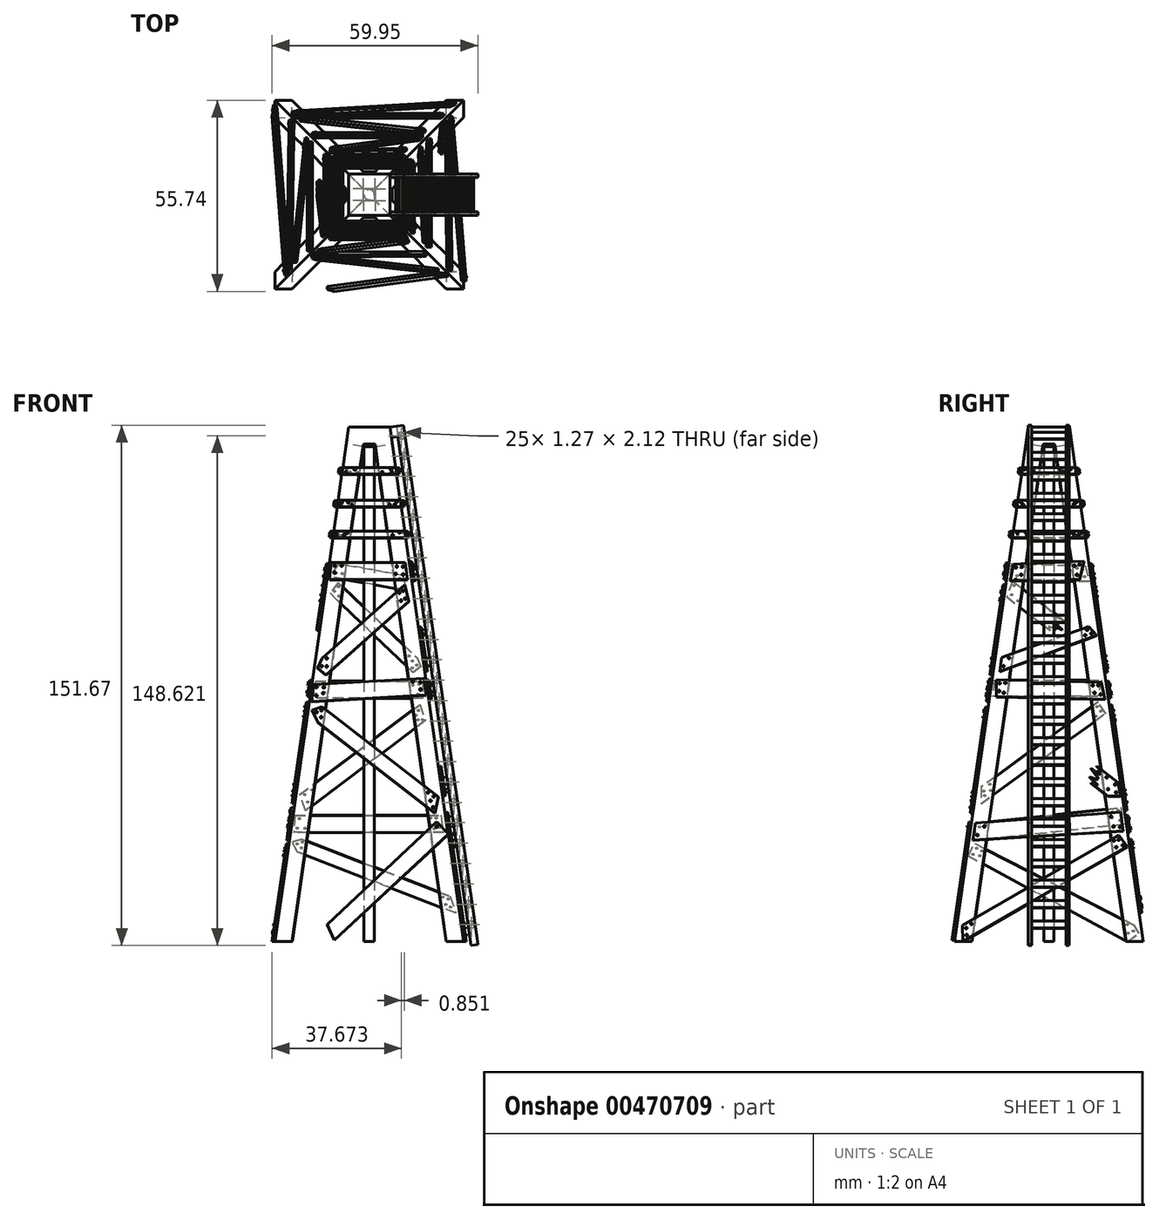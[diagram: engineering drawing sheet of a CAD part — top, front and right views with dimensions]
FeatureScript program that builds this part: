
annotation { "Feature Type Name" : "Feature", "Feature Type Description" : "" }
export const myFeature = defineFeature(function(context is Context, id is Id, definition is map)
    precondition{}
    {
        {
            var Q0;
            Q0=qCreatedBy(makeId("Top.planeOp"),FACE);
            var sketch = newSketch(context, id + "F0", { "sketchPlane" : qUnion([Q0])});
            skCircle(sketch, "E0", {"center": v(-37.37, 36.77) * mm, "radius": 1.5 * mm});
            skSolve(sketch);
        }
        {
            var Q0;
            Q0 = qSketchRegion(id + "F0", true);
            extrude(context, id + "F1", {"entities" : qUnion([Q0]), "depth" : 150 * mm});
        }
        {
            var Q0;
            Q0=makeQuery(id+"F1.opExtrude","CAP_FACE",FACE,{"disambiguationData":[OSD([sQuery(id+"F0.wireOp",EDGE,"E0")])],"isStart":true});
            var sketch = newSketch(context, id + "F2", { "sketchPlane" : qUnion([Q0])});
            skLineSegment(sketch, "E1.bottom", {"start": v(-64.87, -9.27) * mm, "end": v(-9.87, -9.27) * mm});
            skLineSegment(sketch, "E1.top", {"start": v(-64.87, -64.27) * mm, "end": v(-9.87, -64.27) * mm});
            skLineSegment(sketch, "E1.left", {"start": v(-64.87, -9.27) * mm, "end": v(-64.87, -64.27) * mm});
            skLineSegment(sketch, "E1.right", {"start": v(-9.87, -9.27) * mm, "end": v(-9.87, -64.27) * mm});
            skPoint(sketch, "E1.middle", {"position": v(-37.37, -36.77) * mm});
            skSolve(sketch);
        }
        {
            var Q0;
            Q0=makeQuery(id+"F1.opExtrude","CAP_FACE",FACE,{"disambiguationData":[OSD([sQuery(id+"F0.wireOp",EDGE,"E0")])],"isStart":false});
            var sketch = newSketch(context, id + "F3", { "sketchPlane" : qUnion([Q0])});
            skLineSegment(sketch, "E2.bottom", {"start": v(-43.37, 42.77) * mm, "end": v(-31.37, 42.77) * mm});
            skLineSegment(sketch, "E2.top", {"start": v(-43.37, 30.77) * mm, "end": v(-31.37, 30.77) * mm});
            skLineSegment(sketch, "E2.left", {"start": v(-43.37, 42.77) * mm, "end": v(-43.37, 30.77) * mm});
            skLineSegment(sketch, "E2.right", {"start": v(-31.37, 42.77) * mm, "end": v(-31.37, 30.77) * mm});
            skPoint(sketch, "E2.middle", {"position": v(-37.37, 36.77) * mm});
            skSolve(sketch);
        }
        {
            var Q1;
            Q1 = qSketchRegion(id + "F2", true);
            var Q2;
            Q2 = qSketchRegion(id + "F3", true);
            loft(context, id + "F4", {"operationType" : NewBodyOperationType.ADD, "sheetProfilesArray" : [{ "sheetProfileEntities" : qUnion([Q1]) }, { "sheetProfileEntities" : qUnion([Q2]) }]});
        }
        {
            var Q0;
            Q0=makeQuery(id+"F4.opLoft","CAP_FACE",FACE,{"disambiguationData":[OSD([makeQuery(id+"F2.imprint","IMPRINT",FACE,{"disambiguationData":[TD([[makeQuery(id+"F2.imprint","IMPRINT",EDGE,{"derivedFrom":makeQuery(id+"F1.opExtrude","CAP_EDGE",EDGE,{"disambiguationData":[OSD([sQuery(id+"F0.wireOp",EDGE,"E0")])],"isStart":true})}),-1.0]])]})])],"isStart":true});
            shell(context, id + "F5", {"entities" : qUnion([Q0]), "thickness" : 5 * mm});
        }
        {
            var Q0;
            Q0=makeQuery(id+"F4.opLoft","SWEPT_FACE",FACE,{"disambiguationData":[OSD([sQuery(id+"F2.wireOp",EDGE,"E1.bottom"),sQuery(id+"F2.wireOp",EDGE,"E1.left"),sQuery(id+"F2.wireOp",EDGE,"E1.right"),sQuery(id+"F3.wireOp",EDGE,"E2.top"),sQuery(id+"F3.wireOp",EDGE,"E2.left"),sQuery(id+"F3.wireOp",EDGE,"E2.right")])]});
            var sketch = newSketch(context, id + "F6", { "sketchPlane" : qUnion([Q0])});
            skLineSegment(sketch, "E3", {"start": v(-64.87, 1.31) * mm, "end": v(-59.87, 1.31) * mm});
            skLineSegment(sketch, "E4", {"start": v(-9.87, 1.31) * mm, "end": v(-14.87, 1.31) * mm});
            skLineSegment(sketch, "E5", {"start": v(-43.37, 152.85) * mm, "end": v(-31.37, 152.85) * mm});
            skLineSegment(sketch, "E6", {"start": v(-39.08, 147.9) * mm, "end": v(-35.67, 147.9) * mm});
            skLineSegment(sketch, "E7", {"start": v(-64.87, 1.31) * mm, "end": v(-43.37, 152.85) * mm});
            skLineSegment(sketch, "E8", {"start": v(-31.37, 152.85) * mm, "end": v(-9.87, 1.31) * mm});
            skLineSegment(sketch, "E9", {"start": v(-39.08, 147.9) * mm, "end": v(-59.87, 1.31) * mm});
            skLineSegment(sketch, "E10", {"start": v(-35.67, 147.9) * mm, "end": v(-14.87, 1.31) * mm});
            skSolve(sketch);
        }
        {
            var Q0;
            Q0=makeQuery(id+"F6.imprint","IMPRINT",FACE,{"disambiguationData":[TD([[makeQuery(id+"F6.imprint","IMPRINT",EDGE,{"derivedFrom":sQuery(id+"F6.wireOp",EDGE,"E6")}),-1.0]])]});
            var Q1;
            Q1=makeQuery(id+"F5.opShell","OFFSET_FACE",FACE,{"disambiguationData":[OSD([sQuery(id+"F2.wireOp",EDGE,"E1.bottom"),sQuery(id+"F2.wireOp",EDGE,"E1.left"),sQuery(id+"F2.wireOp",EDGE,"E1.right"),sQuery(id+"F3.wireOp",EDGE,"E2.top"),sQuery(id+"F3.wireOp",EDGE,"E2.left"),sQuery(id+"F3.wireOp",EDGE,"E2.right")])]});
            extrude(context, id + "F7", {"entities" : qUnion([Q0]), "operationType" : NewBodyOperationType.REMOVE, "endBound" : BoundingType.UP_TO_SURFACE, "oppositeDirection" : true, "endBoundEntityFace" : qUnion([Q1]), "depth" : 25 * mm});
        }
        {
            var Q0;
            Q0=makeQuery(id+"F4.opLoft","SWEPT_FACE",FACE,{"disambiguationData":[OSD([sQuery(id+"F2.wireOp",EDGE,"E1.bottom"),sQuery(id+"F2.wireOp",EDGE,"E1.top"),sQuery(id+"F2.wireOp",EDGE,"E1.left"),sQuery(id+"F3.wireOp",EDGE,"E2.bottom"),sQuery(id+"F3.wireOp",EDGE,"E2.top"),sQuery(id+"F3.wireOp",EDGE,"E2.left")])]});
            var sketch = newSketch(context, id + "F8", { "sketchPlane" : qUnion([Q0])});
            skLineSegment(sketch, "E11", {"start": v(-64.27, -9.2) * mm, "end": v(-59.27, -9.2) * mm});
            skLineSegment(sketch, "E12", {"start": v(-9.27, -9.2) * mm, "end": v(-14.27, -9.2) * mm});
            skLineSegment(sketch, "E13", {"start": v(-42.77, 142.33) * mm, "end": v(-30.77, 142.33) * mm});
            skLineSegment(sketch, "E14", {"start": v(-38.47, 137.38) * mm, "end": v(-35.06, 137.38) * mm});
            skLineSegment(sketch, "E15", {"start": v(-42.77, 142.33) * mm, "end": v(-64.27, -9.2) * mm});
            skLineSegment(sketch, "E16", {"start": v(-30.77, 142.33) * mm, "end": v(-9.27, -9.2) * mm});
            skLineSegment(sketch, "E17", {"start": v(-59.27, -9.2) * mm, "end": v(-38.47, 137.38) * mm});
            skLineSegment(sketch, "E18", {"start": v(-35.06, 137.38) * mm, "end": v(-14.27, -9.2) * mm});
            skSolve(sketch);
        }
        {
            var Q0;
            Q0=makeQuery(id+"F8.imprint","IMPRINT",FACE,{"disambiguationData":[TD([[makeQuery(id+"F8.imprint","IMPRINT",EDGE,{"derivedFrom":sQuery(id+"F8.wireOp",EDGE,"E14")}),-1.0]])]});
            var Q1;
            Q1=makeQuery(id+"F5.opShell","OFFSET_FACE",FACE,{"disambiguationData":[OSD([sQuery(id+"F2.wireOp",EDGE,"E1.bottom"),sQuery(id+"F2.wireOp",EDGE,"E1.top"),sQuery(id+"F2.wireOp",EDGE,"E1.left"),sQuery(id+"F3.wireOp",EDGE,"E2.bottom"),sQuery(id+"F3.wireOp",EDGE,"E2.top"),sQuery(id+"F3.wireOp",EDGE,"E2.left")])]});
            extrude(context, id + "F9", {"entities" : qUnion([Q0]), "operationType" : NewBodyOperationType.REMOVE, "endBound" : BoundingType.UP_TO_SURFACE, "oppositeDirection" : true, "endBoundEntityFace" : qUnion([Q1]), "depth" : 25 * mm});
        }
        {
            var Q0;
            Q0=makeQuery(id+"F4.opLoft","SWEPT_FACE",FACE,{"disambiguationData":[OSD([sQuery(id+"F2.wireOp",EDGE,"E1.top"),sQuery(id+"F2.wireOp",EDGE,"E1.left"),sQuery(id+"F2.wireOp",EDGE,"E1.right"),sQuery(id+"F3.wireOp",EDGE,"E2.bottom"),sQuery(id+"F3.wireOp",EDGE,"E2.left"),sQuery(id+"F3.wireOp",EDGE,"E2.right")])]});
            var sketch = newSketch(context, id + "F10", { "sketchPlane" : qUnion([Q0])});
            skLineSegment(sketch, "E19", {"start": v(9.87, -9.12) * mm, "end": v(14.87, -9.12) * mm});
            skLineSegment(sketch, "E20", {"start": v(64.87, -9.12) * mm, "end": v(59.87, -9.12) * mm});
            skLineSegment(sketch, "E21", {"start": v(31.37, 142.41) * mm, "end": v(43.37, 142.41) * mm});
            skLineSegment(sketch, "E22", {"start": v(35.67, 137.46) * mm, "end": v(39.08, 137.46) * mm});
            skLineSegment(sketch, "E23", {"start": v(9.87, -9.12) * mm, "end": v(31.37, 142.41) * mm});
            skLineSegment(sketch, "E24", {"start": v(43.37, 142.41) * mm, "end": v(64.87, -9.12) * mm});
            skLineSegment(sketch, "E25", {"start": v(35.67, 137.46) * mm, "end": v(14.87, -9.12) * mm});
            skLineSegment(sketch, "E26", {"start": v(39.08, 137.46) * mm, "end": v(59.87, -9.12) * mm});
            skSolve(sketch);
        }
        {
            var Q0;
            Q0=makeQuery(id+"F10.imprint","IMPRINT",FACE,{"disambiguationData":[TD([[makeQuery(id+"F10.imprint","IMPRINT",EDGE,{"derivedFrom":sQuery(id+"F10.wireOp",EDGE,"E22")}),-1.0]])]});
            var Q1;
            Q1=makeQuery(id+"F5.opShell","OFFSET_FACE",FACE,{"disambiguationData":[OSD([sQuery(id+"F2.wireOp",EDGE,"E1.top"),sQuery(id+"F2.wireOp",EDGE,"E1.left"),sQuery(id+"F2.wireOp",EDGE,"E1.right"),sQuery(id+"F3.wireOp",EDGE,"E2.bottom"),sQuery(id+"F3.wireOp",EDGE,"E2.left"),sQuery(id+"F3.wireOp",EDGE,"E2.right")])]});
            extrude(context, id + "F11", {"entities" : qUnion([Q0]), "operationType" : NewBodyOperationType.REMOVE, "endBound" : BoundingType.UP_TO_SURFACE, "oppositeDirection" : true, "endBoundEntityFace" : qUnion([Q1]), "depth" : 25 * mm});
        }
        {
            var Q0;
            Q0=makeQuery(id+"F4.opLoft","SWEPT_FACE",FACE,{"disambiguationData":[OSD([sQuery(id+"F2.wireOp",EDGE,"E1.bottom"),sQuery(id+"F2.wireOp",EDGE,"E1.top"),sQuery(id+"F2.wireOp",EDGE,"E1.right"),sQuery(id+"F3.wireOp",EDGE,"E2.bottom"),sQuery(id+"F3.wireOp",EDGE,"E2.top"),sQuery(id+"F3.wireOp",EDGE,"E2.right")])]});
            var sketch = newSketch(context, id + "F12", { "sketchPlane" : qUnion([Q0])});
            skLineSegment(sketch, "E27", {"start": v(9.27, 1.4) * mm, "end": v(14.27, 1.4) * mm});
            skLineSegment(sketch, "E28", {"start": v(64.27, 1.4) * mm, "end": v(59.27, 1.4) * mm});
            skLineSegment(sketch, "E29", {"start": v(30.77, 152.93) * mm, "end": v(42.77, 152.93) * mm});
            skLineSegment(sketch, "E30", {"start": v(35.06, 147.98) * mm, "end": v(38.47, 147.98) * mm});
            skLineSegment(sketch, "E31", {"start": v(30.77, 152.93) * mm, "end": v(9.27, 1.4) * mm});
            skLineSegment(sketch, "E32", {"start": v(42.77, 152.93) * mm, "end": v(64.27, 1.4) * mm});
            skLineSegment(sketch, "E33", {"start": v(35.06, 147.98) * mm, "end": v(14.27, 1.4) * mm});
            skLineSegment(sketch, "E34", {"start": v(38.47, 147.98) * mm, "end": v(59.27, 1.4) * mm});
            skSolve(sketch);
        }
        {
            var Q0;
            Q0=makeQuery(id+"F12.imprint","IMPRINT",FACE,{"disambiguationData":[TD([[makeQuery(id+"F12.imprint","IMPRINT",EDGE,{"derivedFrom":sQuery(id+"F12.wireOp",EDGE,"E30")}),-1.0]])]});
            var Q1;
            Q1=makeQuery(id+"F5.opShell","OFFSET_FACE",FACE,{"disambiguationData":[OSD([sQuery(id+"F2.wireOp",EDGE,"E1.bottom"),sQuery(id+"F2.wireOp",EDGE,"E1.top"),sQuery(id+"F2.wireOp",EDGE,"E1.right"),sQuery(id+"F3.wireOp",EDGE,"E2.bottom"),sQuery(id+"F3.wireOp",EDGE,"E2.top"),sQuery(id+"F3.wireOp",EDGE,"E2.right")])]});
            extrude(context, id + "F13", {"entities" : qUnion([Q0]), "operationType" : NewBodyOperationType.REMOVE, "endBound" : BoundingType.UP_TO_SURFACE, "oppositeDirection" : true, "endBoundEntityFace" : qUnion([Q1]), "depth" : 25 * mm});
        }
        {
            var Q0;
            Q0 = qSketchRegion(id + "F0", true);
            extrude(context, id + "F14", {"entities" : qUnion([Q0]), "operationType" : NewBodyOperationType.ADD, "depth" : 150 * mm});
        }
        {
            var Q0;
            Q0=makeQuery(id+"F4.opLoft","SWEPT_FACE",FACE,{"disambiguationData":[OSD([sQuery(id+"F2.wireOp",EDGE,"E1.bottom"),sQuery(id+"F2.wireOp",EDGE,"E1.left"),sQuery(id+"F2.wireOp",EDGE,"E1.right"),sQuery(id+"F3.wireOp",EDGE,"E2.top"),sQuery(id+"F3.wireOp",EDGE,"E2.left"),sQuery(id+"F3.wireOp",EDGE,"E2.right")])]});
            var sketch = newSketch(context, id + "F15", { "sketchPlane" : qUnion([Q0])});
            skLineSegment(sketch, "E35", {"start": v(-9.87, 1.31) * mm, "end": v(-14.35, 32.9) * mm});
            skLineSegment(sketch, "E36", {"start": v(-14.35, 32.9) * mm, "end": v(-47.57, 1.7) * mm});
            skLineSegment(sketch, "E37", {"start": v(-47.57, 1.7) * mm, "end": v(-49.63, 6.26) * mm});
            skLineSegment(sketch, "E38", {"start": v(-14.35, 32.9) * mm, "end": v(-17.78, 36.54) * mm});
            skLineSegment(sketch, "E39", {"start": v(-49.63, 6.26) * mm, "end": v(-17.78, 36.54) * mm});
            skLineSegment(sketch, "E40", {"start": v(-21.42, 78.8) * mm, "end": v(-53.52, 76.95) * mm});
            skLineSegment(sketch, "E41", {"start": v(-21.42, 78.8) * mm, "end": v(-20.71, 73.85) * mm});
            skLineSegment(sketch, "E42", {"start": v(-53.52, 76.95) * mm, "end": v(-54.22, 72) * mm});
            skLineSegment(sketch, "E43", {"start": v(-54.22, 72) * mm, "end": v(-20.71, 73.85) * mm});
            skLineSegment(sketch, "E44", {"start": v(-26.87, 112.86) * mm, "end": v(-48.41, 112.86) * mm});
            skLineSegment(sketch, "E45", {"start": v(-26.87, 112.86) * mm, "end": v(-26.17, 107.9) * mm});
            skLineSegment(sketch, "E46", {"start": v(-26.17, 107.9) * mm, "end": v(-48.96, 107.9) * mm});
            skLineSegment(sketch, "E47", {"start": v(-48.41, 112.86) * mm, "end": v(-48.96, 107.9) * mm});
            skLineSegment(sketch, "E48", {"start": v(-48, 120.19) * mm, "end": v(-26.74, 120.19) * mm});
            skLineSegment(sketch, "E49", {"start": v(-48, 120.19) * mm, "end": v(-47.73, 122.17) * mm});
            skLineSegment(sketch, "E50", {"start": v(-47.73, 122.17) * mm, "end": v(-27.02, 122.17) * mm});
            skLineSegment(sketch, "E51", {"start": v(-27.02, 122.17) * mm, "end": v(-26.74, 120.19) * mm});
            skLineSegment(sketch, "E52", {"start": v(-46.72, 129.27) * mm, "end": v(-28.03, 129.27) * mm});
            skLineSegment(sketch, "E53", {"start": v(-46.72, 129.27) * mm, "end": v(-46.44, 131.25) * mm});
            skLineSegment(sketch, "E54", {"start": v(-46.44, 131.25) * mm, "end": v(-28.3, 131.25) * mm});
            skLineSegment(sketch, "E55", {"start": v(-28.3, 131.25) * mm, "end": v(-28.03, 129.27) * mm});
            skLineSegment(sketch, "E56", {"start": v(-45.35, 138.9) * mm, "end": v(-29.4, 138.9) * mm});
            skLineSegment(sketch, "E57", {"start": v(-45.35, 138.9) * mm, "end": v(-45.07, 140.88) * mm});
            skLineSegment(sketch, "E58", {"start": v(-45.07, 140.88) * mm, "end": v(-29.68, 140.88) * mm});
            skLineSegment(sketch, "E59", {"start": v(-29.68, 140.88) * mm, "end": v(-29.4, 138.9) * mm});
            skSolve(sketch);
        }
        {
            var Q0;
            {var subQ0=sQuery(id+"F15.wireOp",EDGE,"E47");Q0=makeQuery(id+"F15.imprint","IMPRINT",FACE,{"disambiguationData":[TD([[makeQuery(id+"F15.imprint","IMPRINT",EDGE,{"derivedFrom":subQ0}),1.0]])]});}
            var Q1;
            {var subQ0=sQuery(id+"F15.wireOp",EDGE,"E44");var subQ1=makeQuery(id+"F7.boolean.opBoolean","COPY",EDGE,{"derivedFrom":makeQuery(id+"F7.opExtrude","CAP_EDGE",EDGE,{"disambiguationData":[OSD([sQuery(id+"F6.wireOp",EDGE,"E10")])],"isStart":true})});var subQ2=makeQuery(id+"F15.imprint","INTERSECT",VERTEX,{"derivedFrom":[subQ1,subQ0]});Q1=makeQuery(id+"F15.imprint","IMPRINT",FACE,{"disambiguationData":[TD([[makeQuery(id+"F15.imprint","IMPRINT",EDGE,{"disambiguationData":[TD([[subQ2,-1.0]])],"derivedFrom":subQ0}),1.0]])]});}
            var Q2;
            {var subQ0=sQuery(id+"F15.wireOp",EDGE,"E45");Q2=makeQuery(id+"F15.imprint","IMPRINT",FACE,{"disambiguationData":[TD([[makeQuery(id+"F15.imprint","IMPRINT",EDGE,{"derivedFrom":subQ0}),-1.0]])]});}
            var Q3;
            {var subQ0=sQuery(id+"F15.wireOp",EDGE,"E42");Q3=makeQuery(id+"F15.imprint","IMPRINT",FACE,{"disambiguationData":[TD([[makeQuery(id+"F15.imprint","IMPRINT",EDGE,{"derivedFrom":subQ0}),1.0]])]});}
            var Q4;
            {var subQ0=sQuery(id+"F15.wireOp",EDGE,"E40");var subQ1=makeQuery(id+"F7.boolean.opBoolean","COPY",EDGE,{"derivedFrom":makeQuery(id+"F7.opExtrude","CAP_EDGE",EDGE,{"disambiguationData":[OSD([sQuery(id+"F6.wireOp",EDGE,"E10")])],"isStart":true})});var subQ2=makeQuery(id+"F15.imprint","INTERSECT",VERTEX,{"derivedFrom":[subQ1,subQ0]});Q4=makeQuery(id+"F15.imprint","IMPRINT",FACE,{"disambiguationData":[TD([[makeQuery(id+"F15.imprint","IMPRINT",EDGE,{"disambiguationData":[TD([[subQ2,-1.0]])],"derivedFrom":subQ0}),1.0]])]});}
            var Q5;
            {var subQ0=sQuery(id+"F15.wireOp",EDGE,"E41");Q5=makeQuery(id+"F15.imprint","IMPRINT",FACE,{"disambiguationData":[TD([[makeQuery(id+"F15.imprint","IMPRINT",EDGE,{"derivedFrom":subQ0}),-1.0]])]});}
            var Q6;
            {var subQ0=sQuery(id+"F15.wireOp",EDGE,"E37");Q6=makeQuery(id+"F15.imprint","IMPRINT",FACE,{"disambiguationData":[TD([[makeQuery(id+"F15.imprint","IMPRINT",EDGE,{"derivedFrom":subQ0}),-1.0]])]});}
            var Q7;
            {var subQ0=sQuery(id+"F15.wireOp",EDGE,"E38");Q7=makeQuery(id+"F15.imprint","IMPRINT",FACE,{"disambiguationData":[TD([[makeQuery(id+"F15.imprint","IMPRINT",EDGE,{"derivedFrom":subQ0}),1.0]])]});}
            var Q8;
            {var subQ0=sQuery(id+"F15.wireOp",EDGE,"E49");Q8=makeQuery(id+"F15.imprint","IMPRINT",FACE,{"disambiguationData":[TD([[makeQuery(id+"F15.imprint","IMPRINT",EDGE,{"derivedFrom":subQ0}),-1.0]])]});}
            var Q9;
            {var subQ0=sQuery(id+"F15.wireOp",EDGE,"E48");var subQ1=makeQuery(id+"F7.boolean.opBoolean","COPY",EDGE,{"derivedFrom":makeQuery(id+"F7.opExtrude","CAP_EDGE",EDGE,{"disambiguationData":[OSD([sQuery(id+"F6.wireOp",EDGE,"E9")])],"isStart":true})});var subQ2=makeQuery(id+"F15.imprint","INTERSECT",VERTEX,{"derivedFrom":[subQ1,subQ0]});Q9=makeQuery(id+"F15.imprint","IMPRINT",FACE,{"disambiguationData":[TD([[makeQuery(id+"F15.imprint","IMPRINT",EDGE,{"disambiguationData":[TD([[subQ2,-1.0]])],"derivedFrom":subQ0}),1.0]])]});}
            var Q10;
            {var subQ0=sQuery(id+"F15.wireOp",EDGE,"E51");Q10=makeQuery(id+"F15.imprint","IMPRINT",FACE,{"disambiguationData":[TD([[makeQuery(id+"F15.imprint","IMPRINT",EDGE,{"derivedFrom":subQ0}),1.0]])]});}
            var Q11;
            {var subQ0=sQuery(id+"F15.wireOp",EDGE,"E53");Q11=makeQuery(id+"F15.imprint","IMPRINT",FACE,{"disambiguationData":[TD([[makeQuery(id+"F15.imprint","IMPRINT",EDGE,{"derivedFrom":subQ0}),-1.0]])]});}
            var Q12;
            {var subQ0=sQuery(id+"F15.wireOp",EDGE,"E52");var subQ1=makeQuery(id+"F7.boolean.opBoolean","COPY",EDGE,{"derivedFrom":makeQuery(id+"F7.opExtrude","CAP_EDGE",EDGE,{"disambiguationData":[OSD([sQuery(id+"F6.wireOp",EDGE,"E9")])],"isStart":true})});var subQ2=makeQuery(id+"F15.imprint","INTERSECT",VERTEX,{"derivedFrom":[subQ1,subQ0]});Q12=makeQuery(id+"F15.imprint","IMPRINT",FACE,{"disambiguationData":[TD([[makeQuery(id+"F15.imprint","IMPRINT",EDGE,{"disambiguationData":[TD([[subQ2,-1.0]])],"derivedFrom":subQ0}),1.0]])]});}
            var Q13;
            {var subQ0=sQuery(id+"F15.wireOp",EDGE,"E55");Q13=makeQuery(id+"F15.imprint","IMPRINT",FACE,{"disambiguationData":[TD([[makeQuery(id+"F15.imprint","IMPRINT",EDGE,{"derivedFrom":subQ0}),1.0]])]});}
            var Q14;
            {var subQ0=sQuery(id+"F15.wireOp",EDGE,"E57");Q14=makeQuery(id+"F15.imprint","IMPRINT",FACE,{"disambiguationData":[TD([[makeQuery(id+"F15.imprint","IMPRINT",EDGE,{"derivedFrom":subQ0}),-1.0]])]});}
            var Q15;
            {var subQ0=sQuery(id+"F15.wireOp",EDGE,"E56");var subQ1=makeQuery(id+"F7.boolean.opBoolean","COPY",EDGE,{"derivedFrom":makeQuery(id+"F7.opExtrude","CAP_EDGE",EDGE,{"disambiguationData":[OSD([sQuery(id+"F6.wireOp",EDGE,"E9")])],"isStart":true})});var subQ2=makeQuery(id+"F15.imprint","INTERSECT",VERTEX,{"derivedFrom":[subQ1,subQ0]});Q15=makeQuery(id+"F15.imprint","IMPRINT",FACE,{"disambiguationData":[TD([[makeQuery(id+"F15.imprint","IMPRINT",EDGE,{"disambiguationData":[TD([[subQ2,-1.0]])],"derivedFrom":subQ0}),1.0]])]});}
            var Q16;
            {var subQ0=sQuery(id+"F15.wireOp",EDGE,"E59");Q16=makeQuery(id+"F15.imprint","IMPRINT",FACE,{"disambiguationData":[TD([[makeQuery(id+"F15.imprint","IMPRINT",EDGE,{"derivedFrom":subQ0}),1.0]])]});}
            extrude(context, id + "F16", {"entities" : qUnion([Q0, Q1, Q2, Q3, Q4, Q5, Q6, Q7, Q8, Q9, Q10, Q11, Q12, Q13, Q14, Q15, Q16]), "operationType" : NewBodyOperationType.ADD, "depth" : 0.8 * mm});
        }
        {
            var Q0;
            Q0=makeQuery(id+"F4.opLoft","SWEPT_FACE",FACE,{"disambiguationData":[OSD([sQuery(id+"F2.wireOp",EDGE,"E1.bottom"),sQuery(id+"F2.wireOp",EDGE,"E1.top"),sQuery(id+"F2.wireOp",EDGE,"E1.left"),sQuery(id+"F3.wireOp",EDGE,"E2.bottom"),sQuery(id+"F3.wireOp",EDGE,"E2.top"),sQuery(id+"F3.wireOp",EDGE,"E2.left")])]});
            var sketch = newSketch(context, id + "F17", { "sketchPlane" : qUnion([Q0])});
            skLineSegment(sketch, "E60", {"start": v(-15.02, 25.49) * mm, "end": v(-57.78, 30.21) * mm});
            skLineSegment(sketch, "E61", {"start": v(-57.78, 30.21) * mm, "end": v(-58.49, 25.26) * mm});
            skLineSegment(sketch, "E62", {"start": v(-58.49, 25.26) * mm, "end": v(-15.56, 20.52) * mm});
            skLineSegment(sketch, "E63", {"start": v(-15.02, 25.49) * mm, "end": v(-15.56, 20.52) * mm});
            skLineSegment(sketch, "E64", {"start": v(-20.88, 67.78) * mm, "end": v(-52.23, 67.78) * mm});
            skLineSegment(sketch, "E65", {"start": v(-52.23, 67.78) * mm, "end": v(-50.92, 62.95) * mm});
            skLineSegment(sketch, "E66", {"start": v(-50.92, 62.95) * mm, "end": v(-20.37, 62.95) * mm});
            skLineSegment(sketch, "E67", {"start": v(-20.88, 67.78) * mm, "end": v(-20.37, 62.95) * mm});
            skLineSegment(sketch, "E68", {"start": v(-25.76, 102.04) * mm, "end": v(-47.41, 101.43) * mm});
            skLineSegment(sketch, "E69", {"start": v(-47.41, 101.43) * mm, "end": v(-48.5, 96.8) * mm});
            skLineSegment(sketch, "E70", {"start": v(-48.5, 96.8) * mm, "end": v(-25.2, 97.46) * mm});
            skLineSegment(sketch, "E71", {"start": v(-25.76, 102.04) * mm, "end": v(-25.2, 97.46) * mm});
            skLineSegment(sketch, "E72", {"start": v(-26.13, 109.67) * mm, "end": v(-47.4, 109.67) * mm});
            skLineSegment(sketch, "E73", {"start": v(-47.4, 109.67) * mm, "end": v(-47.12, 111.65) * mm});
            skLineSegment(sketch, "E74", {"start": v(-47.12, 111.65) * mm, "end": v(-26.41, 111.65) * mm});
            skLineSegment(sketch, "E75", {"start": v(-26.41, 111.65) * mm, "end": v(-26.13, 109.67) * mm});
            skLineSegment(sketch, "E76", {"start": v(-27.42, 118.75) * mm, "end": v(-46.11, 118.75) * mm});
            skLineSegment(sketch, "E77", {"start": v(-46.11, 118.75) * mm, "end": v(-45.83, 120.73) * mm});
            skLineSegment(sketch, "E78", {"start": v(-45.83, 120.73) * mm, "end": v(-27.7, 120.73) * mm});
            skLineSegment(sketch, "E79", {"start": v(-27.7, 120.73) * mm, "end": v(-27.42, 118.75) * mm});
            skLineSegment(sketch, "E80", {"start": v(-28.79, 128.38) * mm, "end": v(-44.74, 128.38) * mm});
            skLineSegment(sketch, "E81", {"start": v(-44.74, 128.38) * mm, "end": v(-44.46, 130.36) * mm});
            skLineSegment(sketch, "E82", {"start": v(-44.46, 130.36) * mm, "end": v(-29.07, 130.36) * mm});
            skLineSegment(sketch, "E83", {"start": v(-29.07, 130.36) * mm, "end": v(-28.79, 128.38) * mm});
            skSolve(sketch);
        }
        {
            var Q0;
            {var subQ0=sQuery(id+"F17.wireOp",EDGE,"E61");Q0=makeQuery(id+"F17.imprint","IMPRINT",FACE,{"disambiguationData":[TD([[makeQuery(id+"F17.imprint","IMPRINT",EDGE,{"derivedFrom":subQ0}),1.0]])]});}
            var Q1;
            {var subQ0=sQuery(id+"F17.wireOp",EDGE,"E60");var subQ1=makeQuery(id+"F9.boolean.opBoolean","COPY",EDGE,{"derivedFrom":makeQuery(id+"F9.opExtrude","CAP_EDGE",EDGE,{"disambiguationData":[OSD([sQuery(id+"F8.wireOp",EDGE,"E18")])],"isStart":true})});var subQ2=makeQuery(id+"F17.imprint","INTERSECT",VERTEX,{"derivedFrom":[subQ1,subQ0]});Q1=makeQuery(id+"F17.imprint","IMPRINT",FACE,{"disambiguationData":[TD([[makeQuery(id+"F17.imprint","IMPRINT",EDGE,{"disambiguationData":[TD([[subQ2,-1.0]])],"derivedFrom":subQ0}),1.0]])]});}
            var Q2;
            {var subQ0=sQuery(id+"F17.wireOp",EDGE,"E63");Q2=makeQuery(id+"F17.imprint","IMPRINT",FACE,{"disambiguationData":[TD([[makeQuery(id+"F17.imprint","IMPRINT",EDGE,{"derivedFrom":subQ0}),-1.0]])]});}
            var Q3;
            {var subQ0=sQuery(id+"F17.wireOp",EDGE,"E67");Q3=makeQuery(id+"F17.imprint","IMPRINT",FACE,{"disambiguationData":[TD([[makeQuery(id+"F17.imprint","IMPRINT",EDGE,{"derivedFrom":subQ0}),-1.0]])]});}
            var Q4;
            {var subQ0=sQuery(id+"F17.wireOp",EDGE,"E64");var subQ1=makeQuery(id+"F9.boolean.opBoolean","COPY",EDGE,{"derivedFrom":makeQuery(id+"F9.opExtrude","CAP_EDGE",EDGE,{"disambiguationData":[OSD([sQuery(id+"F8.wireOp",EDGE,"E18")])],"isStart":true})});var subQ2=makeQuery(id+"F17.imprint","INTERSECT",VERTEX,{"derivedFrom":[subQ1,subQ0]});Q4=makeQuery(id+"F17.imprint","IMPRINT",FACE,{"disambiguationData":[TD([[makeQuery(id+"F17.imprint","IMPRINT",EDGE,{"disambiguationData":[TD([[subQ2,-1.0]])],"derivedFrom":subQ0}),1.0]])]});}
            var Q5;
            {var subQ0=sQuery(id+"F17.wireOp",EDGE,"E65");Q5=makeQuery(id+"F17.imprint","IMPRINT",FACE,{"disambiguationData":[TD([[makeQuery(id+"F17.imprint","IMPRINT",EDGE,{"derivedFrom":subQ0}),1.0]])]});}
            var Q6;
            {var subQ0=sQuery(id+"F17.wireOp",EDGE,"E69");Q6=makeQuery(id+"F17.imprint","IMPRINT",FACE,{"disambiguationData":[TD([[makeQuery(id+"F17.imprint","IMPRINT",EDGE,{"derivedFrom":subQ0}),1.0]])]});}
            var Q7;
            {var subQ0=sQuery(id+"F17.wireOp",EDGE,"E68");var subQ1=makeQuery(id+"F9.boolean.opBoolean","COPY",EDGE,{"derivedFrom":makeQuery(id+"F9.opExtrude","CAP_EDGE",EDGE,{"disambiguationData":[OSD([sQuery(id+"F8.wireOp",EDGE,"E18")])],"isStart":true})});var subQ2=makeQuery(id+"F17.imprint","INTERSECT",VERTEX,{"derivedFrom":[subQ1,subQ0]});Q7=makeQuery(id+"F17.imprint","IMPRINT",FACE,{"disambiguationData":[TD([[makeQuery(id+"F17.imprint","IMPRINT",EDGE,{"disambiguationData":[TD([[subQ2,-1.0]])],"derivedFrom":subQ0}),1.0]])]});}
            var Q8;
            {var subQ0=sQuery(id+"F17.wireOp",EDGE,"E71");Q8=makeQuery(id+"F17.imprint","IMPRINT",FACE,{"disambiguationData":[TD([[makeQuery(id+"F17.imprint","IMPRINT",EDGE,{"derivedFrom":subQ0}),-1.0]])]});}
            var Q9;
            {var subQ0=sQuery(id+"F17.wireOp",EDGE,"E73");Q9=makeQuery(id+"F17.imprint","IMPRINT",FACE,{"disambiguationData":[TD([[makeQuery(id+"F17.imprint","IMPRINT",EDGE,{"derivedFrom":subQ0}),-1.0]])]});}
            var Q10;
            {var subQ0=sQuery(id+"F17.wireOp",EDGE,"E72");var subQ1=makeQuery(id+"F9.boolean.opBoolean","COPY",EDGE,{"derivedFrom":makeQuery(id+"F9.opExtrude","CAP_EDGE",EDGE,{"disambiguationData":[OSD([sQuery(id+"F8.wireOp",EDGE,"E18")])],"isStart":true})});var subQ2=makeQuery(id+"F17.imprint","INTERSECT",VERTEX,{"derivedFrom":[subQ1,subQ0]});Q10=makeQuery(id+"F17.imprint","IMPRINT",FACE,{"disambiguationData":[TD([[makeQuery(id+"F17.imprint","IMPRINT",EDGE,{"disambiguationData":[TD([[subQ2,-1.0]])],"derivedFrom":subQ0}),-1.0]])]});}
            var Q11;
            {var subQ0=sQuery(id+"F17.wireOp",EDGE,"E75");Q11=makeQuery(id+"F17.imprint","IMPRINT",FACE,{"disambiguationData":[TD([[makeQuery(id+"F17.imprint","IMPRINT",EDGE,{"derivedFrom":subQ0}),1.0]])]});}
            var Q12;
            {var subQ0=sQuery(id+"F17.wireOp",EDGE,"E77");Q12=makeQuery(id+"F17.imprint","IMPRINT",FACE,{"disambiguationData":[TD([[makeQuery(id+"F17.imprint","IMPRINT",EDGE,{"derivedFrom":subQ0}),-1.0]])]});}
            var Q13;
            {var subQ0=sQuery(id+"F17.wireOp",EDGE,"E76");var subQ1=makeQuery(id+"F9.boolean.opBoolean","COPY",EDGE,{"derivedFrom":makeQuery(id+"F9.opExtrude","CAP_EDGE",EDGE,{"disambiguationData":[OSD([sQuery(id+"F8.wireOp",EDGE,"E18")])],"isStart":true})});var subQ2=makeQuery(id+"F17.imprint","INTERSECT",VERTEX,{"derivedFrom":[subQ1,subQ0]});Q13=makeQuery(id+"F17.imprint","IMPRINT",FACE,{"disambiguationData":[TD([[makeQuery(id+"F17.imprint","IMPRINT",EDGE,{"disambiguationData":[TD([[subQ2,-1.0]])],"derivedFrom":subQ0}),-1.0]])]});}
            var Q14;
            {var subQ0=sQuery(id+"F17.wireOp",EDGE,"E79");Q14=makeQuery(id+"F17.imprint","IMPRINT",FACE,{"disambiguationData":[TD([[makeQuery(id+"F17.imprint","IMPRINT",EDGE,{"derivedFrom":subQ0}),1.0]])]});}
            var Q15;
            {var subQ0=sQuery(id+"F17.wireOp",EDGE,"E81");Q15=makeQuery(id+"F17.imprint","IMPRINT",FACE,{"disambiguationData":[TD([[makeQuery(id+"F17.imprint","IMPRINT",EDGE,{"derivedFrom":subQ0}),-1.0]])]});}
            var Q16;
            {var subQ0=sQuery(id+"F17.wireOp",EDGE,"E80");var subQ1=makeQuery(id+"F9.boolean.opBoolean","COPY",EDGE,{"derivedFrom":makeQuery(id+"F9.opExtrude","CAP_EDGE",EDGE,{"disambiguationData":[OSD([sQuery(id+"F8.wireOp",EDGE,"E18")])],"isStart":true})});var subQ2=makeQuery(id+"F17.imprint","INTERSECT",VERTEX,{"derivedFrom":[subQ1,subQ0]});Q16=makeQuery(id+"F17.imprint","IMPRINT",FACE,{"disambiguationData":[TD([[makeQuery(id+"F17.imprint","IMPRINT",EDGE,{"disambiguationData":[TD([[subQ2,-1.0]])],"derivedFrom":subQ0}),-1.0]])]});}
            var Q17;
            {var subQ0=sQuery(id+"F17.wireOp",EDGE,"E83");Q17=makeQuery(id+"F17.imprint","IMPRINT",FACE,{"disambiguationData":[TD([[makeQuery(id+"F17.imprint","IMPRINT",EDGE,{"derivedFrom":subQ0}),1.0]])]});}
            extrude(context, id + "F18", {"entities" : qUnion([Q0, Q1, Q2, Q3, Q4, Q5, Q6, Q7, Q8, Q9, Q10, Q11, Q12, Q13, Q14, Q15, Q16, Q17]), "operationType" : NewBodyOperationType.ADD, "depth" : 0.8 * mm});
        }
        {
            var Q0;
            Q0=makeQuery(id+"F4.opLoft","SWEPT_FACE",FACE,{"disambiguationData":[OSD([sQuery(id+"F2.wireOp",EDGE,"E1.top"),sQuery(id+"F2.wireOp",EDGE,"E1.left"),sQuery(id+"F2.wireOp",EDGE,"E1.right"),sQuery(id+"F3.wireOp",EDGE,"E2.bottom"),sQuery(id+"F3.wireOp",EDGE,"E2.left"),sQuery(id+"F3.wireOp",EDGE,"E2.right")])]});
            var sketch = newSketch(context, id + "F19", { "sketchPlane" : qUnion([Q0])});
            skLineSegment(sketch, "E84", {"start": v(46.27, 102.21) * mm, "end": v(27.68, 98.87) * mm});
            skLineSegment(sketch, "E85", {"start": v(27.68, 98.87) * mm, "end": v(26.47, 94.32) * mm});
            skLineSegment(sketch, "E86", {"start": v(26.47, 94.32) * mm, "end": v(48.86, 98.34) * mm});
            skLineSegment(sketch, "E87", {"start": v(46.27, 102.21) * mm, "end": v(48.86, 98.34) * mm});
            skLineSegment(sketch, "E88", {"start": v(53, 67.55) * mm, "end": v(21.83, 67.55) * mm});
            skLineSegment(sketch, "E89", {"start": v(21.83, 67.55) * mm, "end": v(21.83, 62.51) * mm});
            skLineSegment(sketch, "E90", {"start": v(21.83, 62.51) * mm, "end": v(54.02, 62.51) * mm});
            skLineSegment(sketch, "E91", {"start": v(53, 67.55) * mm, "end": v(54.02, 62.51) * mm});
            skLineSegment(sketch, "E92", {"start": v(58.94, 28.01) * mm, "end": v(16.46, 28.01) * mm});
            skLineSegment(sketch, "E93", {"start": v(16.46, 28.01) * mm, "end": v(15.7, 23.04) * mm});
            skLineSegment(sketch, "E94", {"start": v(15.7, 23.04) * mm, "end": v(59.37, 23.04) * mm});
            skLineSegment(sketch, "E95", {"start": v(58.94, 28.01) * mm, "end": v(59.37, 23.04) * mm});
            skLineSegment(sketch, "E96", {"start": v(48, 109.76) * mm, "end": v(26.74, 109.76) * mm});
            skLineSegment(sketch, "E97", {"start": v(26.74, 109.76) * mm, "end": v(27.02, 111.74) * mm});
            skLineSegment(sketch, "E98", {"start": v(27.02, 111.74) * mm, "end": v(47.73, 111.74) * mm});
            skLineSegment(sketch, "E99", {"start": v(47.73, 111.74) * mm, "end": v(48, 109.76) * mm});
            skLineSegment(sketch, "E100", {"start": v(46.72, 118.84) * mm, "end": v(28.03, 118.84) * mm});
            skLineSegment(sketch, "E101", {"start": v(28.03, 118.84) * mm, "end": v(28.3, 120.82) * mm});
            skLineSegment(sketch, "E102", {"start": v(28.3, 120.82) * mm, "end": v(46.44, 120.82) * mm});
            skLineSegment(sketch, "E103", {"start": v(46.44, 120.82) * mm, "end": v(46.72, 118.84) * mm});
            skLineSegment(sketch, "E104", {"start": v(45.35, 128.47) * mm, "end": v(29.4, 128.47) * mm});
            skLineSegment(sketch, "E105", {"start": v(29.4, 128.47) * mm, "end": v(29.68, 130.45) * mm});
            skLineSegment(sketch, "E106", {"start": v(29.68, 130.45) * mm, "end": v(45.07, 130.45) * mm});
            skLineSegment(sketch, "E107", {"start": v(45.07, 130.45) * mm, "end": v(45.35, 128.47) * mm});
            skSolve(sketch);
        }
        {
            var Q0;
            {var subQ0=sQuery(id+"F19.wireOp",EDGE,"E85");Q0=makeQuery(id+"F19.imprint","IMPRINT",FACE,{"disambiguationData":[TD([[makeQuery(id+"F19.imprint","IMPRINT",EDGE,{"derivedFrom":subQ0}),1.0]])]});}
            var Q1;
            {var subQ0=sQuery(id+"F19.wireOp",EDGE,"E84");var subQ1=makeQuery(id+"F11.boolean.opBoolean","COPY",EDGE,{"derivedFrom":makeQuery(id+"F11.opExtrude","CAP_EDGE",EDGE,{"disambiguationData":[OSD([sQuery(id+"F10.wireOp",EDGE,"E26")])],"isStart":true})});var subQ2=makeQuery(id+"F19.imprint","INTERSECT",VERTEX,{"derivedFrom":[subQ1,subQ0]});Q1=makeQuery(id+"F19.imprint","IMPRINT",FACE,{"disambiguationData":[TD([[makeQuery(id+"F19.imprint","IMPRINT",EDGE,{"disambiguationData":[TD([[subQ2,-1.0]])],"derivedFrom":subQ0}),1.0]])]});}
            var Q2;
            {var subQ0=sQuery(id+"F19.wireOp",EDGE,"E87");Q2=makeQuery(id+"F19.imprint","IMPRINT",FACE,{"disambiguationData":[TD([[makeQuery(id+"F19.imprint","IMPRINT",EDGE,{"derivedFrom":subQ0}),-1.0]])]});}
            var Q3;
            {var subQ0=sQuery(id+"F19.wireOp",EDGE,"E89");Q3=makeQuery(id+"F19.imprint","IMPRINT",FACE,{"disambiguationData":[TD([[makeQuery(id+"F19.imprint","IMPRINT",EDGE,{"derivedFrom":subQ0}),1.0]])]});}
            var Q4;
            {var subQ0=sQuery(id+"F19.wireOp",EDGE,"E88");var subQ1=makeQuery(id+"F11.boolean.opBoolean","COPY",EDGE,{"derivedFrom":makeQuery(id+"F11.opExtrude","CAP_EDGE",EDGE,{"disambiguationData":[OSD([sQuery(id+"F10.wireOp",EDGE,"E26")])],"isStart":true})});var subQ2=makeQuery(id+"F19.imprint","INTERSECT",VERTEX,{"derivedFrom":[subQ1,subQ0]});Q4=makeQuery(id+"F19.imprint","IMPRINT",FACE,{"disambiguationData":[TD([[makeQuery(id+"F19.imprint","IMPRINT",EDGE,{"disambiguationData":[TD([[subQ2,-1.0]])],"derivedFrom":subQ0}),1.0]])]});}
            var Q5;
            {var subQ0=sQuery(id+"F19.wireOp",EDGE,"E91");Q5=makeQuery(id+"F19.imprint","IMPRINT",FACE,{"disambiguationData":[TD([[makeQuery(id+"F19.imprint","IMPRINT",EDGE,{"derivedFrom":subQ0}),-1.0]])]});}
            var Q6;
            {var subQ0=sQuery(id+"F19.wireOp",EDGE,"E93");Q6=makeQuery(id+"F19.imprint","IMPRINT",FACE,{"disambiguationData":[TD([[makeQuery(id+"F19.imprint","IMPRINT",EDGE,{"derivedFrom":subQ0}),1.0]])]});}
            var Q7;
            {var subQ0=sQuery(id+"F19.wireOp",EDGE,"E92");var subQ1=makeQuery(id+"F11.boolean.opBoolean","COPY",EDGE,{"derivedFrom":makeQuery(id+"F11.opExtrude","CAP_EDGE",EDGE,{"disambiguationData":[OSD([sQuery(id+"F10.wireOp",EDGE,"E26")])],"isStart":true})});var subQ2=makeQuery(id+"F19.imprint","INTERSECT",VERTEX,{"derivedFrom":[subQ1,subQ0]});Q7=makeQuery(id+"F19.imprint","IMPRINT",FACE,{"disambiguationData":[TD([[makeQuery(id+"F19.imprint","IMPRINT",EDGE,{"disambiguationData":[TD([[subQ2,-1.0]])],"derivedFrom":subQ0}),1.0]])]});}
            var Q8;
            {var subQ0=sQuery(id+"F19.wireOp",EDGE,"E95");Q8=makeQuery(id+"F19.imprint","IMPRINT",FACE,{"disambiguationData":[TD([[makeQuery(id+"F19.imprint","IMPRINT",EDGE,{"derivedFrom":subQ0}),-1.0]])]});}
            var Q9;
            {var subQ0=sQuery(id+"F19.wireOp",EDGE,"E97");Q9=makeQuery(id+"F19.imprint","IMPRINT",FACE,{"disambiguationData":[TD([[makeQuery(id+"F19.imprint","IMPRINT",EDGE,{"derivedFrom":subQ0}),-1.0]])]});}
            var Q10;
            {var subQ0=sQuery(id+"F19.wireOp",EDGE,"E96");var subQ1=makeQuery(id+"F11.boolean.opBoolean","COPY",EDGE,{"derivedFrom":makeQuery(id+"F11.opExtrude","CAP_EDGE",EDGE,{"disambiguationData":[OSD([sQuery(id+"F10.wireOp",EDGE,"E26")])],"isStart":true})});var subQ2=makeQuery(id+"F19.imprint","INTERSECT",VERTEX,{"derivedFrom":[subQ1,subQ0]});Q10=makeQuery(id+"F19.imprint","IMPRINT",FACE,{"disambiguationData":[TD([[makeQuery(id+"F19.imprint","IMPRINT",EDGE,{"disambiguationData":[TD([[subQ2,-1.0]])],"derivedFrom":subQ0}),-1.0]])]});}
            var Q11;
            {var subQ0=sQuery(id+"F19.wireOp",EDGE,"E99");Q11=makeQuery(id+"F19.imprint","IMPRINT",FACE,{"disambiguationData":[TD([[makeQuery(id+"F19.imprint","IMPRINT",EDGE,{"derivedFrom":subQ0}),1.0]])]});}
            var Q12;
            {var subQ0=sQuery(id+"F19.wireOp",EDGE,"E101");Q12=makeQuery(id+"F19.imprint","IMPRINT",FACE,{"disambiguationData":[TD([[makeQuery(id+"F19.imprint","IMPRINT",EDGE,{"derivedFrom":subQ0}),-1.0]])]});}
            var Q13;
            {var subQ0=sQuery(id+"F19.wireOp",EDGE,"E100");var subQ1=makeQuery(id+"F11.boolean.opBoolean","COPY",EDGE,{"derivedFrom":makeQuery(id+"F11.opExtrude","CAP_EDGE",EDGE,{"disambiguationData":[OSD([sQuery(id+"F10.wireOp",EDGE,"E26")])],"isStart":true})});var subQ2=makeQuery(id+"F19.imprint","INTERSECT",VERTEX,{"derivedFrom":[subQ1,subQ0]});Q13=makeQuery(id+"F19.imprint","IMPRINT",FACE,{"disambiguationData":[TD([[makeQuery(id+"F19.imprint","IMPRINT",EDGE,{"disambiguationData":[TD([[subQ2,-1.0]])],"derivedFrom":subQ0}),-1.0]])]});}
            var Q14;
            {var subQ0=sQuery(id+"F19.wireOp",EDGE,"E103");Q14=makeQuery(id+"F19.imprint","IMPRINT",FACE,{"disambiguationData":[TD([[makeQuery(id+"F19.imprint","IMPRINT",EDGE,{"derivedFrom":subQ0}),1.0]])]});}
            var Q15;
            {var subQ0=sQuery(id+"F19.wireOp",EDGE,"E105");Q15=makeQuery(id+"F19.imprint","IMPRINT",FACE,{"disambiguationData":[TD([[makeQuery(id+"F19.imprint","IMPRINT",EDGE,{"derivedFrom":subQ0}),-1.0]])]});}
            var Q16;
            {var subQ0=sQuery(id+"F19.wireOp",EDGE,"E104");var subQ1=makeQuery(id+"F11.boolean.opBoolean","COPY",EDGE,{"derivedFrom":makeQuery(id+"F11.opExtrude","CAP_EDGE",EDGE,{"disambiguationData":[OSD([sQuery(id+"F10.wireOp",EDGE,"E26")])],"isStart":true})});var subQ2=makeQuery(id+"F19.imprint","INTERSECT",VERTEX,{"derivedFrom":[subQ1,subQ0]});Q16=makeQuery(id+"F19.imprint","IMPRINT",FACE,{"disambiguationData":[TD([[makeQuery(id+"F19.imprint","IMPRINT",EDGE,{"disambiguationData":[TD([[subQ2,-1.0]])],"derivedFrom":subQ0}),-1.0]])]});}
            var Q17;
            {var subQ0=sQuery(id+"F19.wireOp",EDGE,"E107");Q17=makeQuery(id+"F19.imprint","IMPRINT",FACE,{"disambiguationData":[TD([[makeQuery(id+"F19.imprint","IMPRINT",EDGE,{"derivedFrom":subQ0}),1.0]])]});}
            extrude(context, id + "F20", {"entities" : qUnion([Q0, Q1, Q2, Q3, Q4, Q5, Q6, Q7, Q8, Q9, Q10, Q11, Q12, Q13, Q14, Q15, Q16, Q17]), "operationType" : NewBodyOperationType.ADD, "depth" : 0.8 * mm});
        }
        {
            var Q0;
            Q0=makeQuery(id+"F4.opLoft","SWEPT_FACE",FACE,{"disambiguationData":[OSD([sQuery(id+"F2.wireOp",EDGE,"E1.bottom"),sQuery(id+"F2.wireOp",EDGE,"E1.top"),sQuery(id+"F2.wireOp",EDGE,"E1.right"),sQuery(id+"F3.wireOp",EDGE,"E2.bottom"),sQuery(id+"F3.wireOp",EDGE,"E2.top"),sQuery(id+"F3.wireOp",EDGE,"E2.right")])]});
            var sketch = newSketch(context, id + "F21", { "sketchPlane" : qUnion([Q0])});
            skLineSegment(sketch, "E108", {"start": v(15.42, 36.2) * mm, "end": v(57.63, 39.44) * mm});
            skLineSegment(sketch, "E109", {"start": v(15.42, 36.2) * mm, "end": v(14.58, 31.25) * mm});
            skLineSegment(sketch, "E110", {"start": v(14.58, 31.25) * mm, "end": v(58.4, 33.92) * mm});
            skLineSegment(sketch, "E111", {"start": v(57.63, 39.44) * mm, "end": v(58.4, 33.92) * mm});
            skLineSegment(sketch, "E112", {"start": v(21.47, 78.45) * mm, "end": v(21.47, 73.44) * mm});
            skLineSegment(sketch, "E113", {"start": v(21.47, 78.45) * mm, "end": v(52.03, 77.73) * mm});
            skLineSegment(sketch, "E114", {"start": v(21.47, 73.44) * mm, "end": v(53.13, 72.73) * mm});
            skLineSegment(sketch, "E115", {"start": v(52.03, 77.73) * mm, "end": v(53.13, 72.73) * mm});
            skLineSegment(sketch, "E116", {"start": v(26.42, 112.51) * mm, "end": v(25.52, 107.57) * mm});
            skLineSegment(sketch, "E117", {"start": v(26.42, 112.51) * mm, "end": v(46.95, 113.36) * mm});
            skLineSegment(sketch, "E118", {"start": v(46.95, 113.36) * mm, "end": v(45.73, 107.96) * mm});
            skLineSegment(sketch, "E119", {"start": v(25.52, 107.57) * mm, "end": v(45.73, 107.96) * mm});
            skLineSegment(sketch, "E120", {"start": v(47.4, 120.28) * mm, "end": v(26.13, 120.28) * mm});
            skLineSegment(sketch, "E121", {"start": v(26.13, 120.28) * mm, "end": v(26.41, 122.26) * mm});
            skLineSegment(sketch, "E122", {"start": v(26.41, 122.26) * mm, "end": v(47.12, 122.26) * mm});
            skLineSegment(sketch, "E123", {"start": v(47.12, 122.26) * mm, "end": v(47.4, 120.28) * mm});
            skLineSegment(sketch, "E124", {"start": v(45.83, 131.34) * mm, "end": v(46.11, 129.36) * mm});
            skLineSegment(sketch, "E125", {"start": v(46.11, 129.36) * mm, "end": v(27.42, 129.36) * mm});
            skLineSegment(sketch, "E126", {"start": v(27.42, 129.36) * mm, "end": v(27.7, 131.34) * mm});
            skLineSegment(sketch, "E127", {"start": v(27.7, 131.34) * mm, "end": v(45.83, 131.34) * mm});
            skLineSegment(sketch, "E128", {"start": v(44.46, 140.97) * mm, "end": v(44.74, 138.99) * mm});
            skLineSegment(sketch, "E129", {"start": v(44.74, 138.99) * mm, "end": v(28.79, 138.99) * mm});
            skLineSegment(sketch, "E130", {"start": v(28.79, 138.99) * mm, "end": v(29.07, 140.97) * mm});
            skLineSegment(sketch, "E131", {"start": v(29.07, 140.97) * mm, "end": v(44.46, 140.97) * mm});
            skSolve(sketch);
        }
        {
            var Q0;
            {var subQ0=sQuery(id+"F21.wireOp",EDGE,"E116");Q0=makeQuery(id+"F21.imprint","IMPRINT",FACE,{"disambiguationData":[TD([[makeQuery(id+"F21.imprint","IMPRINT",EDGE,{"derivedFrom":subQ0}),1.0]])]});}
            var Q1;
            {var subQ0=sQuery(id+"F21.wireOp",EDGE,"E117");var subQ1=makeQuery(id+"F13.boolean.opBoolean","COPY",EDGE,{"derivedFrom":makeQuery(id+"F13.opExtrude","CAP_EDGE",EDGE,{"disambiguationData":[OSD([sQuery(id+"F12.wireOp",EDGE,"E33")])],"isStart":true})});var subQ2=makeQuery(id+"F21.imprint","INTERSECT",VERTEX,{"derivedFrom":[subQ1,subQ0]});Q1=makeQuery(id+"F21.imprint","IMPRINT",FACE,{"disambiguationData":[TD([[makeQuery(id+"F21.imprint","IMPRINT",EDGE,{"disambiguationData":[TD([[subQ2,-1.0]])],"derivedFrom":subQ0}),-1.0]])]});}
            var Q2;
            {var subQ0=sQuery(id+"F21.wireOp",EDGE,"E118");Q2=makeQuery(id+"F21.imprint","IMPRINT",FACE,{"disambiguationData":[TD([[makeQuery(id+"F21.imprint","IMPRINT",EDGE,{"derivedFrom":subQ0}),-1.0]])]});}
            var Q3;
            {var subQ0=sQuery(id+"F21.wireOp",EDGE,"E112");Q3=makeQuery(id+"F21.imprint","IMPRINT",FACE,{"disambiguationData":[TD([[makeQuery(id+"F21.imprint","IMPRINT",EDGE,{"derivedFrom":subQ0}),1.0]])]});}
            var Q4;
            {var subQ0=sQuery(id+"F21.wireOp",EDGE,"E113");var subQ1=makeQuery(id+"F13.boolean.opBoolean","COPY",EDGE,{"derivedFrom":makeQuery(id+"F13.opExtrude","CAP_EDGE",EDGE,{"disambiguationData":[OSD([sQuery(id+"F12.wireOp",EDGE,"E33")])],"isStart":true})});var subQ2=makeQuery(id+"F21.imprint","INTERSECT",VERTEX,{"derivedFrom":[subQ1,subQ0]});Q4=makeQuery(id+"F21.imprint","IMPRINT",FACE,{"disambiguationData":[TD([[makeQuery(id+"F21.imprint","IMPRINT",EDGE,{"disambiguationData":[TD([[subQ2,-1.0]])],"derivedFrom":subQ0}),-1.0]])]});}
            var Q5;
            {var subQ0=sQuery(id+"F21.wireOp",EDGE,"E115");Q5=makeQuery(id+"F21.imprint","IMPRINT",FACE,{"disambiguationData":[TD([[makeQuery(id+"F21.imprint","IMPRINT",EDGE,{"derivedFrom":subQ0}),-1.0]])]});}
            var Q6;
            {var subQ0=sQuery(id+"F21.wireOp",EDGE,"E109");Q6=makeQuery(id+"F21.imprint","IMPRINT",FACE,{"disambiguationData":[TD([[makeQuery(id+"F21.imprint","IMPRINT",EDGE,{"derivedFrom":subQ0}),1.0]])]});}
            var Q7;
            {var subQ0=sQuery(id+"F21.wireOp",EDGE,"E108");var subQ1=makeQuery(id+"F13.boolean.opBoolean","COPY",EDGE,{"derivedFrom":makeQuery(id+"F13.opExtrude","CAP_EDGE",EDGE,{"disambiguationData":[OSD([sQuery(id+"F12.wireOp",EDGE,"E33")])],"isStart":true})});var subQ2=makeQuery(id+"F21.imprint","INTERSECT",VERTEX,{"derivedFrom":[subQ1,subQ0]});Q7=makeQuery(id+"F21.imprint","IMPRINT",FACE,{"disambiguationData":[TD([[makeQuery(id+"F21.imprint","IMPRINT",EDGE,{"disambiguationData":[TD([[subQ2,-1.0]])],"derivedFrom":subQ0}),-1.0]])]});}
            var Q8;
            {var subQ0=sQuery(id+"F21.wireOp",EDGE,"E111");Q8=makeQuery(id+"F21.imprint","IMPRINT",FACE,{"disambiguationData":[TD([[makeQuery(id+"F21.imprint","IMPRINT",EDGE,{"derivedFrom":subQ0}),-1.0]])]});}
            var Q9;
            {var subQ0=sQuery(id+"F21.wireOp",EDGE,"E130");Q9=makeQuery(id+"F21.imprint","IMPRINT",FACE,{"disambiguationData":[TD([[makeQuery(id+"F21.imprint","IMPRINT",EDGE,{"derivedFrom":subQ0}),-1.0]])]});}
            var Q10;
            {var subQ0=sQuery(id+"F21.wireOp",EDGE,"E129");var subQ1=makeQuery(id+"F13.boolean.opBoolean","COPY",EDGE,{"derivedFrom":makeQuery(id+"F13.opExtrude","CAP_EDGE",EDGE,{"disambiguationData":[OSD([sQuery(id+"F12.wireOp",EDGE,"E34")])],"isStart":true})});var subQ2=makeQuery(id+"F21.imprint","INTERSECT",VERTEX,{"derivedFrom":[subQ1,subQ0]});Q10=makeQuery(id+"F21.imprint","IMPRINT",FACE,{"disambiguationData":[TD([[makeQuery(id+"F21.imprint","IMPRINT",EDGE,{"disambiguationData":[TD([[subQ2,-1.0]])],"derivedFrom":subQ0}),-1.0]])]});}
            var Q11;
            {var subQ0=sQuery(id+"F21.wireOp",EDGE,"E128");Q11=makeQuery(id+"F21.imprint","IMPRINT",FACE,{"disambiguationData":[TD([[makeQuery(id+"F21.imprint","IMPRINT",EDGE,{"derivedFrom":subQ0}),1.0]])]});}
            var Q12;
            {var subQ0=sQuery(id+"F21.wireOp",EDGE,"E126");Q12=makeQuery(id+"F21.imprint","IMPRINT",FACE,{"disambiguationData":[TD([[makeQuery(id+"F21.imprint","IMPRINT",EDGE,{"derivedFrom":subQ0}),-1.0]])]});}
            var Q13;
            {var subQ0=sQuery(id+"F21.wireOp",EDGE,"E125");var subQ1=makeQuery(id+"F13.boolean.opBoolean","COPY",EDGE,{"derivedFrom":makeQuery(id+"F13.opExtrude","CAP_EDGE",EDGE,{"disambiguationData":[OSD([sQuery(id+"F12.wireOp",EDGE,"E34")])],"isStart":true})});var subQ2=makeQuery(id+"F21.imprint","INTERSECT",VERTEX,{"derivedFrom":[subQ1,subQ0]});Q13=makeQuery(id+"F21.imprint","IMPRINT",FACE,{"disambiguationData":[TD([[makeQuery(id+"F21.imprint","IMPRINT",EDGE,{"disambiguationData":[TD([[subQ2,-1.0]])],"derivedFrom":subQ0}),-1.0]])]});}
            var Q14;
            {var subQ0=sQuery(id+"F21.wireOp",EDGE,"E124");Q14=makeQuery(id+"F21.imprint","IMPRINT",FACE,{"disambiguationData":[TD([[makeQuery(id+"F21.imprint","IMPRINT",EDGE,{"derivedFrom":subQ0}),1.0]])]});}
            var Q15;
            {var subQ0=sQuery(id+"F21.wireOp",EDGE,"E121");Q15=makeQuery(id+"F21.imprint","IMPRINT",FACE,{"disambiguationData":[TD([[makeQuery(id+"F21.imprint","IMPRINT",EDGE,{"derivedFrom":subQ0}),-1.0]])]});}
            var Q16;
            {var subQ0=sQuery(id+"F21.wireOp",EDGE,"E120");var subQ1=makeQuery(id+"F13.boolean.opBoolean","COPY",EDGE,{"derivedFrom":makeQuery(id+"F13.opExtrude","CAP_EDGE",EDGE,{"disambiguationData":[OSD([sQuery(id+"F12.wireOp",EDGE,"E34")])],"isStart":true})});var subQ2=makeQuery(id+"F21.imprint","INTERSECT",VERTEX,{"derivedFrom":[subQ1,subQ0]});Q16=makeQuery(id+"F21.imprint","IMPRINT",FACE,{"disambiguationData":[TD([[makeQuery(id+"F21.imprint","IMPRINT",EDGE,{"disambiguationData":[TD([[subQ2,-1.0]])],"derivedFrom":subQ0}),-1.0]])]});}
            var Q17;
            {var subQ0=sQuery(id+"F21.wireOp",EDGE,"E123");Q17=makeQuery(id+"F21.imprint","IMPRINT",FACE,{"disambiguationData":[TD([[makeQuery(id+"F21.imprint","IMPRINT",EDGE,{"derivedFrom":subQ0}),1.0]])]});}
            extrude(context, id + "F22", {"entities" : qUnion([Q0, Q1, Q2, Q3, Q4, Q5, Q6, Q7, Q8, Q9, Q10, Q11, Q12, Q13, Q14, Q15, Q16, Q17]), "operationType" : NewBodyOperationType.ADD, "depth" : 0.8 * mm});
        }
        {
            var Q0;
            {var subQ0=sQuery(id+"F15.wireOp",EDGE,"E47");var subQ1=sQuery(id+"F15.wireOp",EDGE,"E46");var subQ2=sQuery(id+"F15.wireOp",EDGE,"E44");var subQ3=sQuery(id+"F15.wireOp",EDGE,"E43");var subQ4=sQuery(id+"F15.wireOp",EDGE,"E42");var subQ5=sQuery(id+"F15.wireOp",EDGE,"E40");var subQ6=sQuery(id+"F3.wireOp",EDGE,"E2.left");var subQ7=sQuery(id+"F3.wireOp",EDGE,"E2.top");var subQ8=sQuery(id+"F2.wireOp",EDGE,"E1.left");var subQ9=sQuery(id+"F2.wireOp",EDGE,"E1.bottom");var subQ10=sQuery(id+"F0.wireOp",EDGE,"E0");var subQ11=sQuery(id+"F15.wireOp",EDGE,"E48");var subQ12=sQuery(id+"F15.wireOp",EDGE,"E49");Q0=makeQuery(id+"F16.boolean.opBoolean","SPLIT",FACE,{"disambiguationData":[TD([makeQuery(id+"F1.opExtrude","CAP_FACE",FACE,{"disambiguationData":[OSD([subQ10])],"isStart":true}),makeQuery(id+"F4.opLoft","SWEPT_FACE",FACE,{"disambiguationData":[OSD([subQ9,sQuery(id+"F2.wireOp",EDGE,"E1.top"),subQ8,sQuery(id+"F3.wireOp",EDGE,"E2.bottom"),subQ7,subQ6])]}),makeQuery(id+"F4.opLoft","CAP_FACE",FACE,{"disambiguationData":[OSD([makeQuery(id+"F2.imprint","IMPRINT",FACE,{"disambiguationData":[TD([[makeQuery(id+"F2.imprint","IMPRINT",EDGE,{"derivedFrom":makeQuery(id+"F1.opExtrude","CAP_EDGE",EDGE,{"disambiguationData":[OSD([subQ10])],"isStart":true})}),-1.0]])]})])],"isStart":true}),makeQuery(id+"F7.boolean.opBoolean","COPY",FACE,{"derivedFrom":makeQuery(id+"F7.opExtrude","SWEPT_FACE",FACE,{"disambiguationData":[OSD([sQuery(id+"F6.wireOp",EDGE,"E9")])]})}),makeQuery(id+"F16.opExtrude","SWEPT_FACE",FACE,{"disambiguationData":[OSD([subQ5])]}),makeQuery(id+"F16.opExtrude","CAP_FACE",FACE,{"disambiguationData":[OSD([subQ5,sQuery(id+"F15.wireOp",EDGE,"E41"),subQ4,subQ3])],"isStart":true}),makeQuery(id+"F16.opExtrude","SWEPT_FACE",FACE,{"disambiguationData":[OSD([subQ4])]}),makeQuery(id+"F16.opExtrude","SWEPT_FACE",FACE,{"disambiguationData":[OSD([subQ3])]}),makeQuery(id+"F16.opExtrude","SWEPT_FACE",FACE,{"disambiguationData":[OSD([subQ2])]}),makeQuery(id+"F16.opExtrude","CAP_FACE",FACE,{"disambiguationData":[OSD([subQ2,sQuery(id+"F15.wireOp",EDGE,"E45"),subQ1,subQ0])],"isStart":true}),makeQuery(id+"F16.opExtrude","SWEPT_FACE",FACE,{"disambiguationData":[OSD([subQ1])]}),makeQuery(id+"F16.opExtrude","SWEPT_FACE",FACE,{"disambiguationData":[OSD([subQ0])]}),makeQuery(id+"F16.opExtrude","SWEPT_FACE",FACE,{"disambiguationData":[OSD([subQ11])]}),makeQuery(id+"F16.opExtrude","CAP_FACE",FACE,{"disambiguationData":[OSD([subQ11,subQ12,sQuery(id+"F15.wireOp",EDGE,"E50"),sQuery(id+"F15.wireOp",EDGE,"E51")])],"isStart":true}),makeQuery(id+"F16.opExtrude","SWEPT_FACE",FACE,{"disambiguationData":[OSD([subQ12])]})])],"derivedFrom":makeQuery(id+"F4.opLoft","SWEPT_FACE",FACE,{"disambiguationData":[OSD([subQ9,subQ8,sQuery(id+"F2.wireOp",EDGE,"E1.right"),subQ7,subQ6,sQuery(id+"F3.wireOp",EDGE,"E2.right")])]})});}
            var sketch = newSketch(context, id + "F23", { "sketchPlane" : qUnion([Q0])});
            skLineSegment(sketch, "E132", {"start": v(-27, 106.4) * mm, "end": v(-51.18, 84.67) * mm});
            skLineSegment(sketch, "E133", {"start": v(-27, 106.4) * mm, "end": v(-25.8, 101.49) * mm});
            skLineSegment(sketch, "E134", {"start": v(-25.8, 101.49) * mm, "end": v(-49.98, 79.75) * mm});
            skLineSegment(sketch, "E135", {"start": v(-51.18, 84.67) * mm, "end": v(-52.4, 81.85) * mm});
            skLineSegment(sketch, "E136", {"start": v(-52.4, 81.85) * mm, "end": v(-49.98, 79.75) * mm});
            skLineSegment(sketch, "E137", {"start": v(-51.18, 70.44) * mm, "end": v(-17.17, 43.8) * mm});
            skLineSegment(sketch, "E138", {"start": v(-17.17, 43.8) * mm, "end": v(-18.26, 39.14) * mm});
            skLineSegment(sketch, "E139", {"start": v(-18.26, 39.14) * mm, "end": v(-52.25, 65.75) * mm});
            skLineSegment(sketch, "E140", {"start": v(-52.25, 65.75) * mm, "end": v(-54.1, 69.33) * mm});
            skLineSegment(sketch, "E141", {"start": v(-51.18, 70.44) * mm, "end": v(-54.1, 69.33) * mm});
            skSolve(sketch);
        }
        {
            var Q0;
            {var subQ0=sQuery(id+"F23.wireOp",EDGE,"E133");Q0=makeQuery(id+"F23.imprint","IMPRINT",FACE,{"disambiguationData":[TD([[makeQuery(id+"F23.imprint","IMPRINT",EDGE,{"derivedFrom":subQ0}),-1.0]])]});}
            var Q1;
            {var subQ0=sQuery(id+"F23.wireOp",EDGE,"E135");Q1=makeQuery(id+"F23.imprint","IMPRINT",FACE,{"disambiguationData":[TD([[makeQuery(id+"F23.imprint","IMPRINT",EDGE,{"derivedFrom":subQ0}),1.0]])]});}
            var Q2;
            {var subQ0=sQuery(id+"F23.wireOp",EDGE,"E138");Q2=makeQuery(id+"F23.imprint","IMPRINT",FACE,{"disambiguationData":[TD([[makeQuery(id+"F23.imprint","IMPRINT",EDGE,{"derivedFrom":subQ0}),-1.0]])]});}
            var Q3;
            {var subQ1=sQuery(id+"F23.wireOp",EDGE,"E140");Q3=makeQuery(id+"F23.imprint","IMPRINT",FACE,{"disambiguationData":[TD([[makeQuery(id+"F23.imprint","IMPRINT",EDGE,{"derivedFrom":subQ1}),-1.0]])]});}
            extrude(context, id + "F24", {"entities" : qUnion([Q0, Q1, Q2, Q3]), "operationType" : NewBodyOperationType.ADD, "depth" : 0.8 * mm});
        }
        {
            var Q0;
            Q0=makeQuery(id+"F4.opLoft","SWEPT_FACE",FACE,{"disambiguationData":[OSD([sQuery(id+"F2.wireOp",EDGE,"E1.bottom"),sQuery(id+"F2.wireOp",EDGE,"E1.top"),sQuery(id+"F2.wireOp",EDGE,"E1.left"),sQuery(id+"F3.wireOp",EDGE,"E2.bottom"),sQuery(id+"F3.wireOp",EDGE,"E2.top"),sQuery(id+"F3.wireOp",EDGE,"E2.left")])]});
            var sketch = newSketch(context, id + "F25", { "sketchPlane" : qUnion([Q0])});
            skLineSegment(sketch, "E142", {"start": v(-13.15, 16.07) * mm, "end": v(-59.8, -9.2) * mm});
            skLineSegment(sketch, "E143", {"start": v(-59.8, -9.2) * mm, "end": v(-62.96, -6.74) * mm});
            skLineSegment(sketch, "E144", {"start": v(-62.96, -6.74) * mm, "end": v(-61.68, -4.47) * mm});
            skLineSegment(sketch, "E145", {"start": v(-51.08, 61.27) * mm, "end": v(-16.95, 36.24) * mm});
            skLineSegment(sketch, "E146", {"start": v(-16.95, 36.24) * mm, "end": v(-16.95, 31.37) * mm});
            skLineSegment(sketch, "E147", {"start": v(-16.95, 31.37) * mm, "end": v(-53.29, 58.01) * mm});
            skLineSegment(sketch, "E148", {"start": v(-53.29, 58.01) * mm, "end": v(-51.08, 61.27) * mm});
            skLineSegment(sketch, "E149", {"start": v(-26.22, 96.96) * mm, "end": v(-40.97, 85.42) * mm});
            skLineSegment(sketch, "E150", {"start": v(-26.22, 96.96) * mm, "end": v(-24.47, 92.3) * mm});
            skLineSegment(sketch, "E151", {"start": v(-24.47, 92.3) * mm, "end": v(-36.4, 82.96) * mm});
            skLineSegment(sketch, "E152", {"start": v(-40.97, 85.42) * mm, "end": v(-38.02, 86.67) * mm});
            skLineSegment(sketch, "E153", {"start": v(-36.67, 83.62) * mm, "end": v(-37.1, 82.4) * mm});
            skLineSegment(sketch, "E154", {"start": v(-37.1, 82.4) * mm, "end": v(-36.4, 82.96) * mm});
            skLineSegment(sketch, "E155", {"start": v(-13.15, 16.07) * mm, "end": v(-15.07, 19.61) * mm});
            skLineSegment(sketch, "E156", {"start": v(-61.68, -4.47) * mm, "end": v(-15.07, 19.61) * mm});
            skLineSegment(sketch, "E157", {"start": v(-40.7, 82.65) * mm, "end": v(-38.44, 83.56) * mm});
            skLineSegment(sketch, "E158", {"start": v(-38.44, 83.56) * mm, "end": v(-38.87, 82.71) * mm});
            skLineSegment(sketch, "E159", {"start": v(-38.87, 82.71) * mm, "end": v(-36.67, 83.62) * mm});
            skLineSegment(sketch, "E160", {"start": v(-40.7, 82.65) * mm, "end": v(-38.8, 84.33) * mm});
            skLineSegment(sketch, "E161", {"start": v(-38.8, 84.33) * mm, "end": v(-39.6, 84.07) * mm});
            skLineSegment(sketch, "E162", {"start": v(-39.6, 84.07) * mm, "end": v(-38.25, 85.5) * mm});
            skLineSegment(sketch, "E163", {"start": v(-38.25, 85.5) * mm, "end": v(-38.8, 85.5) * mm});
            skLineSegment(sketch, "E164", {"start": v(-38.8, 85.5) * mm, "end": v(-38.02, 86.67) * mm});
            skSolve(sketch);
        }
        {
            var Q0;
            Q0 = qSketchRegion(id + "F25", true);
            extrude(context, id + "F26", {"entities" : qUnion([Q0]), "operationType" : NewBodyOperationType.ADD, "depth" : 0.8 * mm});
        }
        {
            var Q0;
            Q0=makeQuery(id+"F4.opLoft","SWEPT_FACE",FACE,{"disambiguationData":[OSD([sQuery(id+"F2.wireOp",EDGE,"E1.top"),sQuery(id+"F2.wireOp",EDGE,"E1.left"),sQuery(id+"F2.wireOp",EDGE,"E1.right"),sQuery(id+"F3.wireOp",EDGE,"E2.bottom"),sQuery(id+"F3.wireOp",EDGE,"E2.left"),sQuery(id+"F3.wireOp",EDGE,"E2.right")])]});
            var sketch = newSketch(context, id + "F27", { "sketchPlane" : qUnion([Q0])});
            skLineSegment(sketch, "E165", {"start": v(56.92, 21) * mm, "end": v(13.73, 4.16) * mm});
            skLineSegment(sketch, "E166", {"start": v(13.73, 4.16) * mm, "end": v(12.19, -0.71) * mm});
            skLineSegment(sketch, "E167", {"start": v(12.19, -0.71) * mm, "end": v(58.37, 17.3) * mm});
            skLineSegment(sketch, "E168", {"start": v(56.92, 21) * mm, "end": v(59.87, 20.13) * mm});
            skLineSegment(sketch, "E169", {"start": v(59.87, 20.13) * mm, "end": v(58.37, 17.3) * mm});
            skLineSegment(sketch, "E170", {"start": v(55.96, 29.48) * mm, "end": v(57.6, 34.16) * mm});
            skLineSegment(sketch, "E171", {"start": v(57.6, 34.16) * mm, "end": v(22.6, 60.65) * mm});
            skLineSegment(sketch, "E172", {"start": v(22.6, 60.65) * mm, "end": v(20.96, 55.97) * mm});
            skLineSegment(sketch, "E173", {"start": v(20.96, 55.97) * mm, "end": v(55.96, 29.48) * mm});
            skLineSegment(sketch, "E174", {"start": v(46.42, 96.6) * mm, "end": v(23.37, 74.39) * mm});
            skLineSegment(sketch, "E175", {"start": v(22.31, 71.85) * mm, "end": v(24.53, 70.1) * mm});
            skLineSegment(sketch, "E176", {"start": v(24.53, 70.1) * mm, "end": v(48.76, 93.45) * mm});
            skLineSegment(sketch, "E177", {"start": v(46.42, 96.6) * mm, "end": v(48.76, 93.45) * mm});
            skLineSegment(sketch, "E178", {"start": v(22.31, 71.85) * mm, "end": v(23.37, 74.39) * mm});
            skSolve(sketch);
        }
        {
            var Q0;
            {var subQ1=sQuery(id+"F27.wireOp",EDGE,"E175");Q0=makeQuery(id+"F27.imprint","IMPRINT",FACE,{"disambiguationData":[TD([[makeQuery(id+"F27.imprint","IMPRINT",EDGE,{"derivedFrom":subQ1}),1.0]])]});}
            var Q1;
            {var subQ0=sQuery(id+"F27.wireOp",EDGE,"E174");var subQ1=sQuery(id+"F19.wireOp",EDGE,"E86");var subQ2=makeQuery(id+"F20.opExtrude","SWEPT_FACE",FACE,{"disambiguationData":[OSD([subQ1])]});var subQ4=sQuery(id+"F10.wireOp",EDGE,"E26");var subQ5=makeQuery(id+"F11.boolean.opBoolean","COPY",FACE,{"derivedFrom":makeQuery(id+"F11.opExtrude","SWEPT_FACE",FACE,{"disambiguationData":[OSD([subQ4])]})});var subQ6=makeQuery(id+"F4.opLoft","SWEPT_FACE",FACE,{"disambiguationData":[OSD([sQuery(id+"F2.wireOp",EDGE,"E1.top"),sQuery(id+"F2.wireOp",EDGE,"E1.left"),sQuery(id+"F2.wireOp",EDGE,"E1.right"),sQuery(id+"F3.wireOp",EDGE,"E2.bottom"),sQuery(id+"F3.wireOp",EDGE,"E2.left"),sQuery(id+"F3.wireOp",EDGE,"E2.right")])]});var subQ10=makeQuery(id+"F20.boolean.opBoolean","SPLIT",EDGE,{"disambiguationData":[topologyDisambiguationEdgeConnected([subQ6,subQ5]),TD([subQ2])],"derivedFrom":makeQuery(id+"F11.boolean.opBoolean","COPY",EDGE,{"derivedFrom":makeQuery(id+"F11.opExtrude","CAP_EDGE",EDGE,{"disambiguationData":[OSD([subQ4])],"isStart":true})})});var subQ11=makeQuery(id+"F27.imprint","INTERSECT",VERTEX,{"derivedFrom":[subQ10,subQ0]});Q1=makeQuery(id+"F27.imprint","IMPRINT",FACE,{"disambiguationData":[TD([[makeQuery(id+"F27.imprint","IMPRINT",EDGE,{"disambiguationData":[TD([[subQ11,-1.0]])],"derivedFrom":subQ0}),1.0]])]});}
            var Q2;
            {var subQ0=sQuery(id+"F27.wireOp",EDGE,"E177");Q2=makeQuery(id+"F27.imprint","IMPRINT",FACE,{"disambiguationData":[TD([[makeQuery(id+"F27.imprint","IMPRINT",EDGE,{"derivedFrom":subQ0}),-1.0]])]});}
            var Q3;
            {var subQ0=sQuery(id+"F27.wireOp",EDGE,"E172");Q3=makeQuery(id+"F27.imprint","IMPRINT",FACE,{"disambiguationData":[TD([[makeQuery(id+"F27.imprint","IMPRINT",EDGE,{"derivedFrom":subQ0}),1.0]])]});}
            var Q4;
            {var subQ0=sQuery(id+"F27.wireOp",EDGE,"E171");var subQ1=sQuery(id+"F19.wireOp",EDGE,"E90");var subQ2=makeQuery(id+"F20.opExtrude","SWEPT_FACE",FACE,{"disambiguationData":[OSD([subQ1])]});var subQ3=sQuery(id+"F10.wireOp",EDGE,"E26");var subQ4=makeQuery(id+"F11.boolean.opBoolean","COPY",FACE,{"derivedFrom":makeQuery(id+"F11.opExtrude","SWEPT_FACE",FACE,{"disambiguationData":[OSD([subQ3])]})});var subQ5=makeQuery(id+"F4.opLoft","SWEPT_FACE",FACE,{"disambiguationData":[OSD([sQuery(id+"F2.wireOp",EDGE,"E1.top"),sQuery(id+"F2.wireOp",EDGE,"E1.left"),sQuery(id+"F2.wireOp",EDGE,"E1.right"),sQuery(id+"F3.wireOp",EDGE,"E2.bottom"),sQuery(id+"F3.wireOp",EDGE,"E2.left"),sQuery(id+"F3.wireOp",EDGE,"E2.right")])]});var subQ10=makeQuery(id+"F20.boolean.opBoolean","SPLIT",EDGE,{"disambiguationData":[topologyDisambiguationEdgeConnected([subQ5,subQ4]),TD([subQ2])],"derivedFrom":makeQuery(id+"F11.boolean.opBoolean","COPY",EDGE,{"derivedFrom":makeQuery(id+"F11.opExtrude","CAP_EDGE",EDGE,{"disambiguationData":[OSD([subQ3])],"isStart":true})})});var subQ11=makeQuery(id+"F27.imprint","INTERSECT",VERTEX,{"derivedFrom":[subQ10,subQ0]});Q4=makeQuery(id+"F27.imprint","IMPRINT",FACE,{"disambiguationData":[TD([[makeQuery(id+"F27.imprint","IMPRINT",EDGE,{"disambiguationData":[TD([[subQ11,-1.0]])],"derivedFrom":subQ0}),1.0]])]});}
            var Q5;
            {var subQ0=sQuery(id+"F27.wireOp",EDGE,"E170");Q5=makeQuery(id+"F27.imprint","IMPRINT",FACE,{"disambiguationData":[TD([[makeQuery(id+"F27.imprint","IMPRINT",EDGE,{"derivedFrom":subQ0}),1.0]])]});}
            var Q6;
            {var subQ0=sQuery(id+"F27.wireOp",EDGE,"E166");Q6=makeQuery(id+"F27.imprint","IMPRINT",FACE,{"disambiguationData":[TD([[makeQuery(id+"F27.imprint","IMPRINT",EDGE,{"derivedFrom":subQ0}),1.0]])]});}
            var Q7;
            {var subQ0=sQuery(id+"F27.wireOp",EDGE,"E165");var subQ1=sQuery(id+"F0.wireOp",EDGE,"E0");var subQ2=makeQuery(id+"F4.opLoft","CAP_FACE",FACE,{"disambiguationData":[OSD([makeQuery(id+"F2.imprint","IMPRINT",FACE,{"disambiguationData":[TD([[makeQuery(id+"F2.imprint","IMPRINT",EDGE,{"derivedFrom":makeQuery(id+"F1.opExtrude","CAP_EDGE",EDGE,{"disambiguationData":[OSD([subQ1])],"isStart":true})}),-1.0]])]})])],"isStart":true});var subQ3=makeQuery(id+"F4.opLoft","SWEPT_FACE",FACE,{"disambiguationData":[OSD([sQuery(id+"F2.wireOp",EDGE,"E1.top"),sQuery(id+"F2.wireOp",EDGE,"E1.left"),sQuery(id+"F2.wireOp",EDGE,"E1.right"),sQuery(id+"F3.wireOp",EDGE,"E2.bottom"),sQuery(id+"F3.wireOp",EDGE,"E2.left"),sQuery(id+"F3.wireOp",EDGE,"E2.right")])]});var subQ4=sQuery(id+"F10.wireOp",EDGE,"E26");var subQ5=makeQuery(id+"F11.boolean.opBoolean","COPY",FACE,{"derivedFrom":makeQuery(id+"F11.opExtrude","SWEPT_FACE",FACE,{"disambiguationData":[OSD([subQ4])]})});var subQ10=makeQuery(id+"F20.boolean.opBoolean","SPLIT",EDGE,{"disambiguationData":[topologyDisambiguationEdgeConnected([subQ3,subQ5]),TD([subQ2])],"derivedFrom":makeQuery(id+"F11.boolean.opBoolean","COPY",EDGE,{"derivedFrom":makeQuery(id+"F11.opExtrude","CAP_EDGE",EDGE,{"disambiguationData":[OSD([subQ4])],"isStart":true})})});var subQ11=makeQuery(id+"F27.imprint","INTERSECT",VERTEX,{"derivedFrom":[subQ10,subQ0]});Q7=makeQuery(id+"F27.imprint","IMPRINT",FACE,{"disambiguationData":[TD([[makeQuery(id+"F27.imprint","IMPRINT",EDGE,{"disambiguationData":[TD([[subQ11,-1.0]])],"derivedFrom":subQ0}),1.0]])]});}
            var Q8;
            {var subQ1=sQuery(id+"F27.wireOp",EDGE,"E168");Q8=makeQuery(id+"F27.imprint","IMPRINT",FACE,{"disambiguationData":[TD([[makeQuery(id+"F27.imprint","IMPRINT",EDGE,{"derivedFrom":subQ1}),-1.0]])]});}
            extrude(context, id + "F28", {"entities" : qUnion([Q0, Q1, Q2, Q3, Q4, Q5, Q6, Q7, Q8]), "operationType" : NewBodyOperationType.ADD, "depth" : 0.8 * mm});
        }
        {
            var Q0;
            Q0=makeQuery(id+"F4.opLoft","SWEPT_FACE",FACE,{"disambiguationData":[OSD([sQuery(id+"F2.wireOp",EDGE,"E1.bottom"),sQuery(id+"F2.wireOp",EDGE,"E1.top"),sQuery(id+"F2.wireOp",EDGE,"E1.right"),sQuery(id+"F3.wireOp",EDGE,"E2.bottom"),sQuery(id+"F3.wireOp",EDGE,"E2.top"),sQuery(id+"F3.wireOp",EDGE,"E2.right")])]});
            var sketch = newSketch(context, id + "F29", { "sketchPlane" : qUnion([Q0])});
            skLineSegment(sketch, "E179", {"start": v(57.12, 32.68) * mm, "end": v(59.5, 29.3) * mm});
            skLineSegment(sketch, "E180", {"start": v(57.12, 32.68) * mm, "end": v(11.58, 6.1) * mm});
            skLineSegment(sketch, "E181", {"start": v(59.5, 29.3) * mm, "end": v(11.7, 1.4) * mm});
            skLineSegment(sketch, "E182", {"start": v(11.58, 6.1) * mm, "end": v(11.7, 1.4) * mm});
            skLineSegment(sketch, "E183", {"start": v(23.03, 85.04) * mm, "end": v(48.42, 94.12) * mm});
            skLineSegment(sketch, "E184", {"start": v(23.03, 85.04) * mm, "end": v(22.44, 80.87) * mm});
            skLineSegment(sketch, "E185", {"start": v(22.44, 80.87) * mm, "end": v(50.73, 91.54) * mm});
            skLineSegment(sketch, "E186", {"start": v(48.42, 94.12) * mm, "end": v(50.73, 91.54) * mm});
            skLineSegment(sketch, "E187.MirrorCS", {"start": v(48.42, -230.49) * mm, "end": v(50.73, -227.91) * mm});
            skLineSegment(sketch, "E188.MirrorCS", {"start": v(57.12, -169.05) * mm, "end": v(59.5, -165.67) * mm});
            skLineSegment(sketch, "E189", {"start": v(56.88, 48.24) * mm, "end": v(57.63, 44.17) * mm});
            skLineSegment(sketch, "E190", {"start": v(57.63, 44.17) * mm, "end": v(54.01, 44.17) * mm});
            skLineSegment(sketch, "E191", {"start": v(56.88, 48.24) * mm, "end": v(53.29, 51) * mm});
            skLineSegment(sketch, "E192", {"start": v(54.01, 44.17) * mm, "end": v(49.07, 48) * mm});
            skLineSegment(sketch, "E193", {"start": v(49.07, 48) * mm, "end": v(51.01, 47.36) * mm});
            skLineSegment(sketch, "E194", {"start": v(51.01, 47.36) * mm, "end": v(48.6, 49.8) * mm});
            skLineSegment(sketch, "E195", {"start": v(48.6, 49.8) * mm, "end": v(51.01, 49.01) * mm});
            skLineSegment(sketch, "E196", {"start": v(49.07, 52.4) * mm, "end": v(51.75, 50.32) * mm});
            skLineSegment(sketch, "E197", {"start": v(51.75, 50.32) * mm, "end": v(51.01, 51.79) * mm});
            skLineSegment(sketch, "E198", {"start": v(51.01, 51.79) * mm, "end": v(52.13, 51.43) * mm});
            skLineSegment(sketch, "E199", {"start": v(53.29, 51) * mm, "end": v(50.63, 53.06) * mm});
            skLineSegment(sketch, "E200", {"start": v(50.63, 53.06) * mm, "end": v(52.13, 51.43) * mm});
            skLineSegment(sketch, "E201", {"start": v(49.07, 52.4) * mm, "end": v(51.28, 49.3) * mm});
            skLineSegment(sketch, "E202", {"start": v(51.28, 49.3) * mm, "end": v(50.7, 49.62) * mm});
            skLineSegment(sketch, "E203", {"start": v(50.7, 49.62) * mm, "end": v(51.01, 49.01) * mm});
            skSolve(sketch);
        }
        {
            var Q0;
            {var subQ0=sQuery(id+"F29.wireOp",EDGE,"E184");Q0=makeQuery(id+"F29.imprint","IMPRINT",FACE,{"disambiguationData":[TD([[makeQuery(id+"F29.imprint","IMPRINT",EDGE,{"derivedFrom":subQ0}),1.0]])]});}
            var Q1;
            {var subQ0=sQuery(id+"F29.wireOp",EDGE,"E183");var subQ1=sQuery(id+"F21.wireOp",EDGE,"E113");var subQ2=makeQuery(id+"F22.opExtrude","SWEPT_FACE",FACE,{"disambiguationData":[OSD([subQ1])]});var subQ3=sQuery(id+"F12.wireOp",EDGE,"E33");var subQ4=makeQuery(id+"F13.boolean.opBoolean","COPY",FACE,{"derivedFrom":makeQuery(id+"F13.opExtrude","SWEPT_FACE",FACE,{"disambiguationData":[OSD([subQ3])]})});var subQ6=makeQuery(id+"F4.opLoft","SWEPT_FACE",FACE,{"disambiguationData":[OSD([sQuery(id+"F2.wireOp",EDGE,"E1.bottom"),sQuery(id+"F2.wireOp",EDGE,"E1.top"),sQuery(id+"F2.wireOp",EDGE,"E1.right"),sQuery(id+"F3.wireOp",EDGE,"E2.bottom"),sQuery(id+"F3.wireOp",EDGE,"E2.top"),sQuery(id+"F3.wireOp",EDGE,"E2.right")])]});var subQ10=makeQuery(id+"F22.boolean.opBoolean","SPLIT",EDGE,{"disambiguationData":[topologyDisambiguationEdgeConnected([subQ6,subQ4]),TD([subQ2])],"derivedFrom":makeQuery(id+"F13.boolean.opBoolean","COPY",EDGE,{"derivedFrom":makeQuery(id+"F13.opExtrude","CAP_EDGE",EDGE,{"disambiguationData":[OSD([subQ3])],"isStart":true})})});var subQ11=makeQuery(id+"F29.imprint","INTERSECT",VERTEX,{"derivedFrom":[subQ10,subQ0]});Q1=makeQuery(id+"F29.imprint","IMPRINT",FACE,{"disambiguationData":[TD([[makeQuery(id+"F29.imprint","IMPRINT",EDGE,{"disambiguationData":[TD([[subQ11,-1.0]])],"derivedFrom":subQ0}),-1.0]])]});}
            var Q2;
            {var subQ0=sQuery(id+"F29.wireOp",EDGE,"E186");Q2=makeQuery(id+"F29.imprint","IMPRINT",FACE,{"disambiguationData":[TD([[makeQuery(id+"F29.imprint","IMPRINT",EDGE,{"derivedFrom":subQ0}),-1.0]])]});}
            var Q3;
            Q3=makeQuery(id+"F29.imprint","IMPRINT",FACE,{"disambiguationData":[TD([[makeQuery(id+"F29.imprint","IMPRINT",EDGE,{"derivedFrom":sQuery(id+"F29.wireOp",EDGE,"0OS1gCzz-fl7m-p3iD-XObm-fLrfBI6thJWB")}),1.0]])]});
            var Q4;
            {var subQ1=sQuery(id+"F29.wireOp",EDGE,"nBL4PKUQ-QQTe-avk2-rrJt-ASHt1bdKWm2I");Q4=makeQuery(id+"F29.imprint","IMPRINT",FACE,{"disambiguationData":[TD([[makeQuery(id+"F29.imprint","IMPRINT",EDGE,{"derivedFrom":subQ1}),-1.0]])]});}
            var Q5;
            {var subQ0=sQuery(id+"F29.wireOp",EDGE,"id68fQG2-Odk7-nmJ8-34jQ-xtIFyQgMa7tB");var subQ1=sQuery(id+"F29.wireOp",EDGE,"gShwCU95-sFFk-s6Wt-J5Y8-qgkjBtHmKBt2");var subQ2=makeQuery(id+"F29.imprint","INTERSECT",VERTEX,{"derivedFrom":[subQ1,subQ0]});Q5=makeQuery(id+"F29.imprint","IMPRINT",FACE,{"disambiguationData":[TD([[makeQuery(id+"F29.imprint","IMPRINT",EDGE,{"disambiguationData":[TD([[subQ2,1.0]])],"derivedFrom":subQ1}),-1.0]])]});}
            var Q6;
            {var subQ0=sQuery(id+"F29.wireOp",EDGE,"E182");Q6=makeQuery(id+"F29.imprint","IMPRINT",FACE,{"disambiguationData":[TD([[makeQuery(id+"F29.imprint","IMPRINT",EDGE,{"derivedFrom":subQ0}),1.0]])]});}
            var Q7;
            {var subQ0=sQuery(id+"F29.wireOp",EDGE,"E180");var subQ1=sQuery(id+"F12.wireOp",EDGE,"E34");var subQ2=makeQuery(id+"F13.boolean.opBoolean","COPY",FACE,{"derivedFrom":makeQuery(id+"F13.opExtrude","SWEPT_FACE",FACE,{"disambiguationData":[OSD([subQ1])]})});var subQ3=sQuery(id+"F0.wireOp",EDGE,"E0");var subQ4=makeQuery(id+"F4.opLoft","CAP_FACE",FACE,{"disambiguationData":[OSD([makeQuery(id+"F2.imprint","IMPRINT",FACE,{"disambiguationData":[TD([[makeQuery(id+"F2.imprint","IMPRINT",EDGE,{"derivedFrom":makeQuery(id+"F1.opExtrude","CAP_EDGE",EDGE,{"disambiguationData":[OSD([subQ3])],"isStart":true})}),-1.0]])]})])],"isStart":true});var subQ5=makeQuery(id+"F4.opLoft","SWEPT_FACE",FACE,{"disambiguationData":[OSD([sQuery(id+"F2.wireOp",EDGE,"E1.bottom"),sQuery(id+"F2.wireOp",EDGE,"E1.top"),sQuery(id+"F2.wireOp",EDGE,"E1.right"),sQuery(id+"F3.wireOp",EDGE,"E2.bottom"),sQuery(id+"F3.wireOp",EDGE,"E2.top"),sQuery(id+"F3.wireOp",EDGE,"E2.right")])]});var subQ10=makeQuery(id+"F22.boolean.opBoolean","SPLIT",EDGE,{"disambiguationData":[topologyDisambiguationEdgeConnected([subQ5,subQ2]),TD([subQ4])],"derivedFrom":makeQuery(id+"F13.boolean.opBoolean","COPY",EDGE,{"derivedFrom":makeQuery(id+"F13.opExtrude","CAP_EDGE",EDGE,{"disambiguationData":[OSD([subQ1])],"isStart":true})})});var subQ11=makeQuery(id+"F29.imprint","INTERSECT",VERTEX,{"derivedFrom":[subQ10,subQ0]});Q7=makeQuery(id+"F29.imprint","IMPRINT",FACE,{"disambiguationData":[TD([[makeQuery(id+"F29.imprint","IMPRINT",EDGE,{"disambiguationData":[TD([[subQ11,-1.0]])],"derivedFrom":subQ0}),1.0]])]});}
            var Q8;
            {var subQ0=sQuery(id+"F29.wireOp",EDGE,"E179");Q8=makeQuery(id+"F29.imprint","IMPRINT",FACE,{"disambiguationData":[TD([[makeQuery(id+"F29.imprint","IMPRINT",EDGE,{"derivedFrom":subQ0}),-1.0]])]});}
            var Q9;
            Q9=makeQuery(id+"F29.imprint","IMPRINT",FACE,{"disambiguationData":[TD([[makeQuery(id+"F29.imprint","IMPRINT",EDGE,{"derivedFrom":sQuery(id+"F29.wireOp",EDGE,"E189")}),-1.0]])]});
            var Q10;
            {var subQ11=sQuery(id+"F29.wireOp",EDGE,"E193");Q10=makeQuery(id+"F29.imprint","IMPRINT",FACE,{"disambiguationData":[TD([[makeQuery(id+"F29.imprint","IMPRINT",EDGE,{"derivedFrom":subQ11}),-1.0]])]});}
            extrude(context, id + "F30", {"entities" : qUnion([Q0, Q1, Q2, Q3, Q4, Q5, Q6, Q7, Q8, Q9, Q10]), "operationType" : NewBodyOperationType.ADD, "depth" : 0.8 * mm});
        }
        {
            var Q0;
            Q0=makeQuery(id+"F16.opExtrude","CAP_FACE",FACE,{"disambiguationData":[OSD([sQuery(id+"F15.wireOp",EDGE,"E56"),sQuery(id+"F15.wireOp",EDGE,"E57"),sQuery(id+"F15.wireOp",EDGE,"E58"),sQuery(id+"F15.wireOp",EDGE,"E59")])],"isStart":false});
            var sketch = newSketch(context, id + "F31", { "sketchPlane" : qUnion([Q0])});
            skCircle(sketch, "E204", {"center": v(-41.6, 140.28) * mm, "radius": 0.25 * mm});
            skCircle(sketch, "E205", {"center": v(-44.08, 139.5) * mm, "radius": 0.25 * mm});
            skCircle(sketch, "E206", {"center": v(-33.6, 139.47) * mm, "radius": 0.25 * mm});
            skCircle(sketch, "E207", {"center": v(-31.11, 140.37) * mm, "radius": 0.25 * mm});
            skCircle(sketch, "E208", {"center": v(-30.75, 139.5) * mm, "radius": 0.25 * mm});
            skCircle(sketch, "E209", {"center": v(-45.99, 129.83) * mm, "radius": 0.25 * mm});
            skCircle(sketch, "E210", {"center": v(-45.35, 130.66) * mm, "radius": 0.25 * mm});
            skCircle(sketch, "E211", {"center": v(-42.51, 129.78) * mm, "radius": 0.25 * mm});
            skCircle(sketch, "E212", {"center": v(-43.5, 130.6) * mm, "radius": 0.25 * mm});
            skCircle(sketch, "E213", {"center": v(-29.47, 130.7) * mm, "radius": 0.25 * mm});
            skCircle(sketch, "E214", {"center": v(-31.47, 129.95) * mm, "radius": 0.25 * mm});
            skCircle(sketch, "E215", {"center": v(-29.93, 129.93) * mm, "radius": 0.25 * mm});
            skCircle(sketch, "E216", {"center": v(-46.97, 121.45) * mm, "radius": 0.25 * mm});
            skCircle(sketch, "E217", {"center": v(-46.88, 120.75) * mm, "radius": 0.25 * mm});
            skCircle(sketch, "E218", {"center": v(-43.86, 121.57) * mm, "radius": 0.25 * mm});
            skCircle(sketch, "E219", {"center": v(-44.76, 120.92) * mm, "radius": 0.25 * mm});
            skCircle(sketch, "E220", {"center": v(-30.56, 120.9) * mm, "radius": 0.25 * mm});
            skCircle(sketch, "E221", {"center": v(-28.56, 121.77) * mm, "radius": 0.25 * mm});
            skCircle(sketch, "E222", {"center": v(-47.44, 111.95) * mm, "radius": 0.25 * mm});
            skCircle(sketch, "E223", {"center": v(-45.37, 111.95) * mm, "radius": 0.25 * mm});
            skCircle(sketch, "E224", {"center": v(-47.44, 109.87) * mm, "radius": 0.25 * mm});
            skCircle(sketch, "E225", {"center": v(-29.34, 111.68) * mm, "radius": 0.25 * mm});
            skCircle(sketch, "E226", {"center": v(-27.46, 109.32) * mm, "radius": 0.25 * mm});
            skCircle(sketch, "E227", {"center": v(-27.54, 111.64) * mm, "radius": 0.25 * mm});
            skCircle(sketch, "E228", {"center": v(-29.64, 109.52) * mm, "radius": 0.25 * mm});
            skCircle(sketch, "E229", {"center": v(-27.5, 104.53) * mm, "radius": 0.25 * mm});
            skCircle(sketch, "E230", {"center": v(-28.57, 103.95) * mm, "radius": 0.25 * mm});
            skCircle(sketch, "E231", {"center": v(-26.89, 102.25) * mm, "radius": 0.25 * mm});
            skCircle(sketch, "E232", {"center": v(-28.11, 101.63) * mm, "radius": 0.25 * mm});
            skCircle(sketch, "E233", {"center": v(-51.26, 82.38) * mm, "radius": 0.25 * mm});
            skCircle(sketch, "E234", {"center": v(-49.77, 84.66) * mm, "radius": 0.25 * mm});
            skCircle(sketch, "E235", {"center": v(-49.77, 82.27) * mm, "radius": 0.25 * mm});
            skCircle(sketch, "E236", {"center": v(-52.75, 76.2) * mm, "radius": 0.25 * mm});
            skCircle(sketch, "E237", {"center": v(-50.61, 76.12) * mm, "radius": 0.25 * mm});
            skCircle(sketch, "E238", {"center": v(-52.8, 73.65) * mm, "radius": 0.25 * mm});
            skCircle(sketch, "E239", {"center": v(-50.8, 74.38) * mm, "radius": 0.25 * mm});
            skCircle(sketch, "E240", {"center": v(-24.7, 77.78) * mm, "radius": 0.25 * mm});
            skCircle(sketch, "E241", {"center": v(-22.41, 75.46) * mm, "radius": 0.25 * mm});
            skCircle(sketch, "E242", {"center": v(-22.45, 77.63) * mm, "radius": 0.25 * mm});
            skCircle(sketch, "E243", {"center": v(-52.72, 68.85) * mm, "radius": 0.25 * mm});
            skCircle(sketch, "E244", {"center": v(-51.3, 69.4) * mm, "radius": 0.25 * mm});
            skCircle(sketch, "E245", {"center": v(-51.42, 67.27) * mm, "radius": 0.25 * mm});
            skCircle(sketch, "E246", {"center": v(-20.23, 45.16) * mm, "radius": 0.25 * mm});
            skCircle(sketch, "E247", {"center": v(-18.55, 44) * mm, "radius": 0.25 * mm});
            skCircle(sketch, "E248", {"center": v(-18.78, 40.8) * mm, "radius": 0.25 * mm});
            skCircle(sketch, "E249", {"center": v(-19.5, 42.72) * mm, "radius": 0.25 * mm});
            skCircle(sketch, "E250", {"center": v(-17.74, 35.08) * mm, "radius": 0.25 * mm});
            skSolve(sketch);
        }
        {
            var Q0;
            Q0 = qSketchRegion(id + "F31", true);
            extrude(context, id + "F32", {"entities" : qUnion([Q0]), "operationType" : NewBodyOperationType.ADD, "depth" : 0.3 * mm});
        }
        {
            var Q0;
            Q0=makeQuery(id+"F18.opExtrude","CAP_FACE",FACE,{"disambiguationData":[OSD([sQuery(id+"F17.wireOp",EDGE,"E68"),sQuery(id+"F17.wireOp",EDGE,"E69"),sQuery(id+"F17.wireOp",EDGE,"E70"),sQuery(id+"F17.wireOp",EDGE,"E71")])],"isStart":false});
            var sketch = newSketch(context, id + "F33", { "sketchPlane" : qUnion([Q0])});
            skCircle(sketch, "E251", {"center": v(-43.28, 129.8) * mm, "radius": 0.25 * mm});
            skCircle(sketch, "E252", {"center": v(-41.14, 129.11) * mm, "radius": 0.25 * mm});
            skCircle(sketch, "E253", {"center": v(-32.4, 129.62) * mm, "radius": 0.25 * mm});
            skCircle(sketch, "E254", {"center": v(-30.31, 129.67) * mm, "radius": 0.25 * mm});
            skCircle(sketch, "E255", {"center": v(-31.18, 129.07) * mm, "radius": 0.25 * mm});
            skCircle(sketch, "E256", {"center": v(-44.6, 119.87) * mm, "radius": 0.25 * mm});
            skCircle(sketch, "E257", {"center": v(-28.26, 120.24) * mm, "radius": 0.25 * mm});
            skCircle(sketch, "E258", {"center": v(-29.04, 119.28) * mm, "radius": 0.25 * mm});
            skCircle(sketch, "E259", {"center": v(-31.65, 120.24) * mm, "radius": 0.25 * mm});
            skCircle(sketch, "E260", {"center": v(-43.42, 111.1) * mm, "radius": 0.25 * mm});
            skCircle(sketch, "E261", {"center": v(-44.05, 110.27) * mm, "radius": 0.25 * mm});
            skCircle(sketch, "E262", {"center": v(-45.78, 111.14) * mm, "radius": 0.25 * mm});
            skCircle(sketch, "E263", {"center": v(-46.24, 110.27) * mm, "radius": 0.25 * mm});
            skCircle(sketch, "E264", {"center": v(-30.36, 111.05) * mm, "radius": 0.25 * mm});
            skCircle(sketch, "E265", {"center": v(-27.63, 110.27) * mm, "radius": 0.25 * mm});
            skCircle(sketch, "E266", {"center": v(-44.97, 100.63) * mm, "radius": 0.25 * mm});
            skCircle(sketch, "E267", {"center": v(-47.16, 98.18) * mm, "radius": 0.25 * mm});
            skCircle(sketch, "E268", {"center": v(-46.55, 100.2) * mm, "radius": 0.25 * mm});
            skCircle(sketch, "E269", {"center": v(-45.46, 98.42) * mm, "radius": 0.25 * mm});
            skCircle(sketch, "E270", {"center": v(-28.63, 100.81) * mm, "radius": 0.25 * mm});
            skCircle(sketch, "E271", {"center": v(-26.63, 100.63) * mm, "radius": 0.25 * mm});
            skCircle(sketch, "E272", {"center": v(-27.48, 98.42) * mm, "radius": 0.25 * mm});
            skCircle(sketch, "E273", {"center": v(-26.63, 95.6) * mm, "radius": 0.25 * mm});
            skCircle(sketch, "E274", {"center": v(-25.9, 92.84) * mm, "radius": 0.25 * mm});
            skCircle(sketch, "E275", {"center": v(-27.78, 91.06) * mm, "radius": 0.25 * mm});
            skCircle(sketch, "E276", {"center": v(-51.1, 67) * mm, "radius": 0.25 * mm});
            skCircle(sketch, "E277", {"center": v(-50.07, 64.12) * mm, "radius": 0.25 * mm});
            skCircle(sketch, "E278", {"center": v(-49.59, 66.45) * mm, "radius": 0.25 * mm});
            skCircle(sketch, "E279", {"center": v(-23.9, 66.88) * mm, "radius": 0.25 * mm});
            skCircle(sketch, "E280", {"center": v(-22.07, 64.49) * mm, "radius": 0.25 * mm});
            skCircle(sketch, "E281", {"center": v(-50.8, 59.89) * mm, "radius": 0.25 * mm});
            skCircle(sketch, "E282", {"center": v(-50.44, 57.07) * mm, "radius": 0.25 * mm});
            skCircle(sketch, "E283", {"center": v(-51.9, 58.54) * mm, "radius": 0.25 * mm});
            skCircle(sketch, "E284", {"center": v(-19.52, 37) * mm, "radius": 0.25 * mm});
            skCircle(sketch, "E285", {"center": v(-17.76, 35.04) * mm, "radius": 0.25 * mm});
            skCircle(sketch, "E286", {"center": v(-19.82, 35.22) * mm, "radius": 0.25 * mm});
            skCircle(sketch, "E287", {"center": v(-18.06, 33.69) * mm, "radius": 0.25 * mm});
            skCircle(sketch, "E288", {"center": v(-57, 29.33) * mm, "radius": 0.25 * mm});
            skCircle(sketch, "E289", {"center": v(-55.3, 28.9) * mm, "radius": 0.25 * mm});
            skCircle(sketch, "E290", {"center": v(-57.48, 26.39) * mm, "radius": 0.25 * mm});
            skCircle(sketch, "E291", {"center": v(-55.17, 27.12) * mm, "radius": 0.25 * mm});
            skCircle(sketch, "E292", {"center": v(-18.3, 25.04) * mm, "radius": 0.25 * mm});
            skCircle(sketch, "E293", {"center": v(-16.54, 24.48) * mm, "radius": 0.25 * mm});
            skCircle(sketch, "E294", {"center": v(-17.27, 17.37) * mm, "radius": 0.25 * mm});
            skCircle(sketch, "E295", {"center": v(-15.7, 18.16) * mm, "radius": 0.25 * mm});
            skCircle(sketch, "E296", {"center": v(-14.66, 16.38) * mm, "radius": 0.25 * mm});
            skCircle(sketch, "E297", {"center": v(-16.6, 15.95) * mm, "radius": 0.25 * mm});
            skCircle(sketch, "E298", {"center": v(-59.6, -4.3) * mm, "radius": 0.25 * mm});
            skCircle(sketch, "E299", {"center": v(-61.37, -6.2) * mm, "radius": 0.25 * mm});
            skCircle(sketch, "E300", {"center": v(-59.85, -6.81) * mm, "radius": 0.25 * mm});
            skSolve(sketch);
        }
        {
            var Q0;
            Q0 = qSketchRegion(id + "F33", true);
            extrude(context, id + "F34", {"entities" : qUnion([Q0]), "operationType" : NewBodyOperationType.ADD, "depth" : 0.3 * mm});
        }
        {
            var Q0;
            Q0=makeQuery(id+"F20.opExtrude","CAP_FACE",FACE,{"disambiguationData":[OSD([sQuery(id+"F19.wireOp",EDGE,"E88"),sQuery(id+"F19.wireOp",EDGE,"E89"),sQuery(id+"F19.wireOp",EDGE,"E90"),sQuery(id+"F19.wireOp",EDGE,"E91")])],"isStart":false});
            var sketch = newSketch(context, id + "F35", { "sketchPlane" : qUnion([Q0])});
            skCircle(sketch, "E301", {"center": v(30.82, 129.72) * mm, "radius": 0.25 * mm});
            skCircle(sketch, "E302", {"center": v(41.34, 129.77) * mm, "radius": 0.25 * mm});
            skCircle(sketch, "E303", {"center": v(40.78, 128.95) * mm, "radius": 0.25 * mm});
            skCircle(sketch, "E304", {"center": v(43.94, 129.82) * mm, "radius": 0.25 * mm});
            skCircle(sketch, "E305", {"center": v(42.97, 129.1) * mm, "radius": 0.25 * mm});
            skCircle(sketch, "E306", {"center": v(29.18, 120.28) * mm, "radius": 0.25 * mm});
            skCircle(sketch, "E307", {"center": v(31.94, 120.28) * mm, "radius": 0.25 * mm});
            skCircle(sketch, "E308", {"center": v(31.28, 119.4) * mm, "radius": 0.25 * mm});
            skCircle(sketch, "E309", {"center": v(42.26, 120.28) * mm, "radius": 0.25 * mm});
            skCircle(sketch, "E310", {"center": v(45.37, 119.66) * mm, "radius": 0.25 * mm});
            skCircle(sketch, "E311", {"center": v(27.6, 111.2) * mm, "radius": 0.25 * mm});
            skCircle(sketch, "E312", {"center": v(30.4, 110.47) * mm, "radius": 0.25 * mm});
            skCircle(sketch, "E313", {"center": v(43.43, 111.2) * mm, "radius": 0.25 * mm});
            skCircle(sketch, "E314", {"center": v(47.11, 111.2) * mm, "radius": 0.25 * mm});
            skCircle(sketch, "E315", {"center": v(44.66, 110.53) * mm, "radius": 0.25 * mm});
            skCircle(sketch, "E316", {"center": v(46.09, 110.53) * mm, "radius": 0.25 * mm});
            skCircle(sketch, "E317", {"center": v(28.54, 97.77) * mm, "radius": 0.25 * mm});
            skCircle(sketch, "E318", {"center": v(27.65, 95.23) * mm, "radius": 0.25 * mm});
            skCircle(sketch, "E319", {"center": v(45.48, 101.37) * mm, "radius": 0.25 * mm});
            skCircle(sketch, "E320", {"center": v(45.24, 99.16) * mm, "radius": 0.25 * mm});
            skCircle(sketch, "E321", {"center": v(47.1, 99.32) * mm, "radius": 0.25 * mm});
            skCircle(sketch, "E322", {"center": v(46.21, 92.52) * mm, "radius": 0.25 * mm});
            skCircle(sketch, "E323", {"center": v(47.5, 94) * mm, "radius": 0.25 * mm});
            skCircle(sketch, "E324", {"center": v(46.3, 95.3) * mm, "radius": 0.25 * mm});
            skCircle(sketch, "E325", {"center": v(23.51, 72.21) * mm, "radius": 0.25 * mm});
            skCircle(sketch, "E326", {"center": v(24.8, 71.4) * mm, "radius": 0.25 * mm});
            skCircle(sketch, "E327", {"center": v(25.78, 74.91) * mm, "radius": 0.25 * mm});
            skCircle(sketch, "E328", {"center": v(24.8, 73.44) * mm, "radius": 0.25 * mm});
            skCircle(sketch, "E329", {"center": v(22.86, 66.56) * mm, "radius": 0.25 * mm});
            skCircle(sketch, "E330", {"center": v(24.65, 66.31) * mm, "radius": 0.25 * mm});
            skCircle(sketch, "E331", {"center": v(23.19, 63.7) * mm, "radius": 0.25 * mm});
            skCircle(sketch, "E332", {"center": v(50.02, 66.48) * mm, "radius": 0.25 * mm});
            skCircle(sketch, "E333", {"center": v(51.97, 66.4) * mm, "radius": 0.25 * mm});
            skCircle(sketch, "E334", {"center": v(50.43, 64.18) * mm, "radius": 0.25 * mm});
            skCircle(sketch, "E335", {"center": v(53, 63.7) * mm, "radius": 0.25 * mm});
            skCircle(sketch, "E336", {"center": v(23.02, 58.86) * mm, "radius": 0.25 * mm});
            skCircle(sketch, "E337", {"center": v(23.75, 57.47) * mm, "radius": 0.25 * mm});
            skCircle(sketch, "E338", {"center": v(21.83, 56.16) * mm, "radius": 0.25 * mm});
            skCircle(sketch, "E339", {"center": v(23.19, 56.08) * mm, "radius": 0.25 * mm});
            skCircle(sketch, "E340", {"center": v(54.02, 35.44) * mm, "radius": 0.25 * mm});
            skCircle(sketch, "E341", {"center": v(56.19, 34.04) * mm, "radius": 0.25 * mm});
            skCircle(sketch, "E342", {"center": v(55.3, 31.91) * mm, "radius": 0.25 * mm});
            skCircle(sketch, "E343", {"center": v(19.46, 27.16) * mm, "radius": 0.25 * mm});
            skCircle(sketch, "E344", {"center": v(17.84, 27.16) * mm, "radius": 0.25 * mm});
            skCircle(sketch, "E345", {"center": v(18.4, 24.05) * mm, "radius": 0.25 * mm});
            skCircle(sketch, "E346", {"center": v(16.86, 24.38) * mm, "radius": 0.25 * mm});
            skCircle(sketch, "E347", {"center": v(56.1, 24.13) * mm, "radius": 0.25 * mm});
            skCircle(sketch, "E348", {"center": v(58.37, 24.21) * mm, "radius": 0.25 * mm});
            skCircle(sketch, "E349", {"center": v(57.73, 27) * mm, "radius": 0.25 * mm});
            skCircle(sketch, "E350", {"center": v(58.37, 19.55) * mm, "radius": 0.25 * mm});
            skCircle(sketch, "E351", {"center": v(56.83, 20.12) * mm, "radius": 0.25 * mm});
            skCircle(sketch, "E352", {"center": v(57.16, 18.4) * mm, "radius": 0.25 * mm});
            skCircle(sketch, "E353", {"center": v(15.97, 3.9) * mm, "radius": 0.25 * mm});
            skCircle(sketch, "E354", {"center": v(14.35, 3.33) * mm, "radius": 0.25 * mm});
            skCircle(sketch, "E355", {"center": v(13.7, 0.95) * mm, "radius": 0.25 * mm});
            skCircle(sketch, "E356", {"center": v(15.08, 1.7) * mm, "radius": 0.25 * mm});
            skSolve(sketch);
        }
        {
            var Q0;
            Q0 = qSketchRegion(id + "F35", true);
            extrude(context, id + "F36", {"entities" : qUnion([Q0]), "operationType" : NewBodyOperationType.ADD, "depth" : 0.3 * mm});
        }
        {
            var Q0;
            Q0=makeQuery(id+"F22.opExtrude","CAP_FACE",FACE,{"disambiguationData":[OSD([sQuery(id+"F21.wireOp",EDGE,"E116"),sQuery(id+"F21.wireOp",EDGE,"E117"),sQuery(id+"F21.wireOp",EDGE,"E118"),sQuery(id+"F21.wireOp",EDGE,"E119")])],"isStart":false});
            var sketch = newSketch(context, id + "F37", { "sketchPlane" : qUnion([Q0])});
            skCircle(sketch, "E357", {"center": v(29.68, 140.46) * mm, "radius": 0.25 * mm});
            skCircle(sketch, "E358", {"center": v(32.25, 139.77) * mm, "radius": 0.25 * mm});
            skCircle(sketch, "E359", {"center": v(40.03, 140.5) * mm, "radius": 0.25 * mm});
            skCircle(sketch, "E360", {"center": v(42.95, 140.42) * mm, "radius": 0.25 * mm});
            skCircle(sketch, "E361", {"center": v(40.97, 139.64) * mm, "radius": 0.25 * mm});
            skCircle(sketch, "E362", {"center": v(42.18, 139.85) * mm, "radius": 0.25 * mm});
            skCircle(sketch, "E363", {"center": v(28.56, 130.87) * mm, "radius": 0.25 * mm});
            skCircle(sketch, "E364", {"center": v(29.2, 129.96) * mm, "radius": 0.25 * mm});
            skCircle(sketch, "E365", {"center": v(30.8, 130.83) * mm, "radius": 0.25 * mm});
            skCircle(sketch, "E366", {"center": v(31.52, 130.05) * mm, "radius": 0.25 * mm});
            skCircle(sketch, "E367", {"center": v(42.26, 130.83) * mm, "radius": 0.25 * mm});
            skCircle(sketch, "E368", {"center": v(44.84, 130.83) * mm, "radius": 0.25 * mm});
            skCircle(sketch, "E369", {"center": v(44.02, 130.14) * mm, "radius": 0.25 * mm});
            skCircle(sketch, "E370", {"center": v(27.57, 121.67) * mm, "radius": 0.25 * mm});
            skCircle(sketch, "E371", {"center": v(30.06, 121.76) * mm, "radius": 0.25 * mm});
            skCircle(sketch, "E372", {"center": v(30.45, 120.9) * mm, "radius": 0.25 * mm});
            skCircle(sketch, "E373", {"center": v(46.3, 121.76) * mm, "radius": 0.25 * mm});
            skCircle(sketch, "E374", {"center": v(45.31, 121.02) * mm, "radius": 0.25 * mm});
            skCircle(sketch, "E375", {"center": v(42.95, 121.76) * mm, "radius": 0.25 * mm});
            skCircle(sketch, "E376", {"center": v(44.02, 121.33) * mm, "radius": 0.25 * mm});
            skCircle(sketch, "E377", {"center": v(28.95, 111.74) * mm, "radius": 0.25 * mm});
            skCircle(sketch, "E378", {"center": v(27.14, 111.57) * mm, "radius": 0.25 * mm});
            skCircle(sketch, "E379", {"center": v(28.68, 109.35) * mm, "radius": 0.25 * mm});
            skCircle(sketch, "E380", {"center": v(27.09, 107.85) * mm, "radius": 0.25 * mm});
            skCircle(sketch, "E381", {"center": v(45.73, 112.42) * mm, "radius": 0.25 * mm});
            skCircle(sketch, "E382", {"center": v(44.98, 109.3) * mm, "radius": 0.25 * mm});
            skCircle(sketch, "E383", {"center": v(44.21, 112) * mm, "radius": 0.25 * mm});
            skCircle(sketch, "E384", {"center": v(25.17, 84.84) * mm, "radius": 0.25 * mm});
            skCircle(sketch, "E385", {"center": v(23.5, 82.43) * mm, "radius": 0.25 * mm});
            skCircle(sketch, "E386", {"center": v(49.17, 92.05) * mm, "radius": 0.25 * mm});
            skCircle(sketch, "E387", {"center": v(47.37, 91.53) * mm, "radius": 0.25 * mm});
            skCircle(sketch, "E388", {"center": v(47.89, 93.16) * mm, "radius": 0.25 * mm});
            skCircle(sketch, "E389", {"center": v(24.08, 77.56) * mm, "radius": 0.25 * mm});
            skCircle(sketch, "E390", {"center": v(22.4, 77.43) * mm, "radius": 0.25 * mm});
            skCircle(sketch, "E391", {"center": v(22.28, 75.08) * mm, "radius": 0.25 * mm});
            skCircle(sketch, "E392", {"center": v(23.63, 74.56) * mm, "radius": 0.25 * mm});
            skCircle(sketch, "E393", {"center": v(51.17, 76.84) * mm, "radius": 0.25 * mm});
            skCircle(sketch, "E394", {"center": v(49.56, 76.78) * mm, "radius": 0.25 * mm});
            skCircle(sketch, "E395", {"center": v(50.07, 74.56) * mm, "radius": 0.25 * mm});
            skCircle(sketch, "E396", {"center": v(51.88, 74.1) * mm, "radius": 0.25 * mm});
            skCircle(sketch, "E397", {"center": v(17.93, 35.2) * mm, "radius": 0.25 * mm});
            skCircle(sketch, "E398", {"center": v(15.94, 32.65) * mm, "radius": 0.25 * mm});
            skCircle(sketch, "E399", {"center": v(54.81, 38.14) * mm, "radius": 0.25 * mm});
            skCircle(sketch, "E400", {"center": v(57.5, 35.04) * mm, "radius": 0.25 * mm});
            skCircle(sketch, "E401", {"center": v(55.58, 35.2) * mm, "radius": 0.25 * mm});
            skCircle(sketch, "E402", {"center": v(12.65, 5.28) * mm, "radius": 0.25 * mm});
            skCircle(sketch, "E403", {"center": v(12.8, 3.2) * mm, "radius": 0.25 * mm});
            skCircle(sketch, "E404", {"center": v(14.18, 6.52) * mm, "radius": 0.25 * mm});
            skCircle(sketch, "E405", {"center": v(55.73, 31.1) * mm, "radius": 0.25 * mm});
            skCircle(sketch, "E406", {"center": v(58.33, 29.63) * mm, "radius": 0.25 * mm});
            skCircle(sketch, "E407", {"center": v(57.11, 31.33) * mm, "radius": 0.25 * mm});
            skCircle(sketch, "E408", {"center": v(56.42, 29.1) * mm, "radius": 0.25 * mm});
            skCircle(sketch, "E409", {"center": v(56.06, 47.57) * mm, "radius": 0.25 * mm});
            skCircle(sketch, "E410", {"center": v(56.35, 45.24) * mm, "radius": 0.25 * mm});
            skCircle(sketch, "E411", {"center": v(54.04, 46.19) * mm, "radius": 0.25 * mm});
            skCircle(sketch, "E412", {"center": v(53.6, 49.69) * mm, "radius": 0.25 * mm});
            skSolve(sketch);
        }
        {
            var Q0;
            Q0 = qSketchRegion(id + "F37", true);
            extrude(context, id + "F38", {"entities" : qUnion([Q0]), "operationType" : NewBodyOperationType.ADD, "depth" : 0.3 * mm});
        }
        {
            var Q0;
            {var subQ0=sQuery(id+"F0.wireOp",EDGE,"E0");var subQ1=sQuery(id+"F3.wireOp",EDGE,"E2.right");var subQ3=sQuery(id+"F3.wireOp",EDGE,"E2.bottom");var subQ4=sQuery(id+"F2.wireOp",EDGE,"E1.right");var subQ6=sQuery(id+"F2.wireOp",EDGE,"E1.top");var subQ10=sQuery(id+"F3.wireOp",EDGE,"E2.top");var subQ11=sQuery(id+"F2.wireOp",EDGE,"E1.bottom");Q0=makeQuery(id+"F22.boolean.opBoolean","SPLIT",FACE,{"disambiguationData":[TD([makeQuery(id+"F4.opLoft","CAP_FACE",FACE,{"disambiguationData":[OSD([makeQuery(id+"F3.imprint","IMPRINT",FACE,{"disambiguationData":[TD([[makeQuery(id+"F3.imprint","IMPRINT",EDGE,{"derivedFrom":makeQuery(id+"F1.opExtrude","CAP_EDGE",EDGE,{"disambiguationData":[OSD([subQ0])],"isStart":false})}),1.0]])]})])],"isStart":true})])],"derivedFrom":makeQuery(id+"F4.opLoft","SWEPT_FACE",FACE,{"disambiguationData":[OSD([subQ11,subQ6,subQ4,subQ3,subQ10,subQ1])]})});}
            var sketch = newSketch(context, id + "F39", { "sketchPlane" : qUnion([Q0])});
            skLineSegment(sketch, "E413.bottom", {"start": v(30.77, 152.93) * mm, "end": v(31.77, 152.93) * mm});
            skLineSegment(sketch, "E413.top", {"start": v(30.77, 149.93) * mm, "end": v(31.77, 149.93) * mm});
            skLineSegment(sketch, "E413.left", {"start": v(30.77, 152.93) * mm, "end": v(30.77, 149.93) * mm});
            skLineSegment(sketch, "E413.right", {"start": v(31.77, 152.93) * mm, "end": v(31.77, 149.93) * mm});
            skLineSegment(sketch, "E414.bottom", {"start": v(42.77, 152.93) * mm, "end": v(41.77, 152.93) * mm});
            skLineSegment(sketch, "E414.top", {"start": v(42.77, 149.93) * mm, "end": v(41.77, 149.93) * mm});
            skLineSegment(sketch, "E414.left", {"start": v(42.77, 152.93) * mm, "end": v(42.77, 149.93) * mm});
            skLineSegment(sketch, "E414.right", {"start": v(41.77, 152.93) * mm, "end": v(41.77, 149.93) * mm});
            skSolve(sketch);
        }
        {
            var Q0;
            Q0 = qSketchRegion(id + "F39", true);
            extrude(context, id + "F40", {"entities" : qUnion([Q0]), "operationType" : NewBodyOperationType.ADD, "depth" : 2 * mm});
        }
        {
            var Q0;
            Q0=makeQuery(id+"F22.opExtrude","CAP_FACE",FACE,{"disambiguationData":[OSD([sQuery(id+"F21.wireOp",EDGE,"E116"),sQuery(id+"F21.wireOp",EDGE,"E117"),sQuery(id+"F21.wireOp",EDGE,"E118"),sQuery(id+"F21.wireOp",EDGE,"E119")])],"isStart":false});
            var sketch = newSketch(context, id + "F41", { "sketchPlane" : qUnion([Q0])});
            skPoint(sketch, "E415", {"position": v(31.8, 150.14) * mm});
            skPoint(sketch, "E416", {"position": v(41.8, 150.14) * mm});
            skLineSegment(sketch, "E417", {"start": v(31.8, 150.14) * mm, "end": v(31.8, 0) * mm});
            skLineSegment(sketch, "E418", {"start": v(41.8, 150.14) * mm, "end": v(41.8, 0) * mm});
            skLineSegment(sketch, "E419", {"start": v(41.8, 107.89) * mm, "end": v(31.8, 107.89) * mm});
            skLineSegment(sketch, "E420.bottom", {"start": v(31.8, 107.89) * mm, "end": v(30.8, 107.89) * mm});
            skLineSegment(sketch, "E420.top", {"start": v(31.8, 110.89) * mm, "end": v(30.8, 110.89) * mm});
            skLineSegment(sketch, "E420.left", {"start": v(31.8, 107.89) * mm, "end": v(31.8, 110.89) * mm});
            skLineSegment(sketch, "E420.right", {"start": v(30.8, 107.89) * mm, "end": v(30.8, 110.89) * mm});
            skLineSegment(sketch, "E421.bottom", {"start": v(41.8, 107.89) * mm, "end": v(42.8, 107.89) * mm});
            skLineSegment(sketch, "E421.top", {"start": v(41.8, 110.89) * mm, "end": v(42.8, 110.89) * mm});
            skLineSegment(sketch, "E421.left", {"start": v(41.8, 107.89) * mm, "end": v(41.8, 110.89) * mm});
            skLineSegment(sketch, "E421.right", {"start": v(42.8, 107.89) * mm, "end": v(42.8, 110.89) * mm});
            skLineSegment(sketch, "E422", {"start": v(31.8, 73.67) * mm, "end": v(41.8, 73.67) * mm});
            skLineSegment(sketch, "E423.bottom", {"start": v(31.8, 73.67) * mm, "end": v(30.8, 73.67) * mm});
            skLineSegment(sketch, "E423.top", {"start": v(31.8, 76.67) * mm, "end": v(30.8, 76.67) * mm});
            skLineSegment(sketch, "E423.left", {"start": v(31.8, 73.67) * mm, "end": v(31.8, 76.67) * mm});
            skLineSegment(sketch, "E423.right", {"start": v(30.8, 73.67) * mm, "end": v(30.8, 76.67) * mm});
            skLineSegment(sketch, "E424.bottom", {"start": v(41.8, 73.67) * mm, "end": v(42.8, 73.67) * mm});
            skLineSegment(sketch, "E424.top", {"start": v(41.8, 76.67) * mm, "end": v(42.8, 76.67) * mm});
            skLineSegment(sketch, "E424.left", {"start": v(41.8, 73.67) * mm, "end": v(41.8, 76.67) * mm});
            skLineSegment(sketch, "E424.right", {"start": v(42.8, 73.67) * mm, "end": v(42.8, 76.67) * mm});
            skLineSegment(sketch, "E425", {"start": v(41.8, 33.07) * mm, "end": v(31.8, 33.07) * mm});
            skLineSegment(sketch, "E426.bottom", {"start": v(31.8, 33.07) * mm, "end": v(30.8, 33.07) * mm});
            skLineSegment(sketch, "E426.top", {"start": v(31.8, 36.07) * mm, "end": v(30.8, 36.07) * mm});
            skLineSegment(sketch, "E426.left", {"start": v(31.8, 33.07) * mm, "end": v(31.8, 36.07) * mm});
            skLineSegment(sketch, "E426.right", {"start": v(30.8, 33.07) * mm, "end": v(30.8, 36.07) * mm});
            skLineSegment(sketch, "E427.bottom", {"start": v(41.8, 33.07) * mm, "end": v(42.8, 33.07) * mm});
            skLineSegment(sketch, "E427.top", {"start": v(41.8, 36.07) * mm, "end": v(42.8, 36.07) * mm});
            skLineSegment(sketch, "E427.left", {"start": v(41.8, 33.07) * mm, "end": v(41.8, 36.07) * mm});
            skLineSegment(sketch, "E427.right", {"start": v(42.8, 33.07) * mm, "end": v(42.8, 36.07) * mm});
            skSolve(sketch);
        }
        {
            var Q0;
            Q0=makeQuery(id+"F41.imprint","IMPRINT",FACE,{"disambiguationData":[TD([[makeQuery(id+"F41.imprint","IMPRINT",EDGE,{"derivedFrom":sQuery(id+"F41.wireOp",EDGE,"E426.bottom")}),-1.0]])]});
            var Q1;
            Q1=makeQuery(id+"F41.imprint","IMPRINT",FACE,{"disambiguationData":[TD([[makeQuery(id+"F41.imprint","IMPRINT",EDGE,{"derivedFrom":sQuery(id+"F41.wireOp",EDGE,"E427.bottom")}),1.0]])]});
            var Q2;
            Q2=makeQuery(id+"F41.imprint","IMPRINT",FACE,{"disambiguationData":[TD([[makeQuery(id+"F41.imprint","IMPRINT",EDGE,{"derivedFrom":sQuery(id+"F41.wireOp",EDGE,"E423.bottom")}),-1.0]])]});
            var Q3;
            Q3=makeQuery(id+"F41.imprint","IMPRINT",FACE,{"disambiguationData":[TD([[makeQuery(id+"F41.imprint","IMPRINT",EDGE,{"derivedFrom":sQuery(id+"F41.wireOp",EDGE,"E424.bottom")}),1.0]])]});
            var Q4;
            Q4=makeQuery(id+"F41.imprint","IMPRINT",FACE,{"disambiguationData":[TD([[makeQuery(id+"F41.imprint","IMPRINT",EDGE,{"derivedFrom":sQuery(id+"F41.wireOp",EDGE,"E420.bottom")}),-1.0]])]});
            var Q5;
            {var subQ0=sQuery(id+"F41.wireOp",EDGE,"E421.top");Q5=makeQuery(id+"F41.imprint","IMPRINT",FACE,{"disambiguationData":[TD([[makeQuery(id+"F41.imprint","IMPRINT",EDGE,{"derivedFrom":subQ0}),-1.0]])]});}
            extrude(context, id + "F42", {"entities" : qUnion([Q0, Q1, Q2, Q3, Q4, Q5]), "operationType" : NewBodyOperationType.ADD, "depth" : 1.2 * mm});
        }
        {
            var Q0;
            Q0=makeQuery(id+"F40.opExtrude","CAP_FACE",FACE,{"disambiguationData":[OSD([sQuery(id+"F39.wireOp",EDGE,"E413.bottom"),sQuery(id+"F39.wireOp",EDGE,"E413.top"),sQuery(id+"F39.wireOp",EDGE,"E413.left"),sQuery(id+"F39.wireOp",EDGE,"E413.right")])],"isStart":false});
            var sketch = newSketch(context, id + "F43", { "sketchPlane" : qUnion([Q0])});
            skPoint(sketch, "E428", {"position": v(30.77, 152.93) * mm});
            skLineSegment(sketch, "E429.bottom", {"start": v(30.77, 152.93) * mm, "end": v(31.77, 152.93) * mm});
            skLineSegment(sketch, "E429.top", {"start": v(30.77, 0) * mm, "end": v(31.77, 0) * mm});
            skLineSegment(sketch, "E429.left", {"start": v(30.77, 152.93) * mm, "end": v(30.77, 0) * mm});
            skLineSegment(sketch, "E429.right", {"start": v(31.77, 152.93) * mm, "end": v(31.77, 0) * mm});
            skPoint(sketch, "E430", {"position": v(42.74, 152.94) * mm});
            skLineSegment(sketch, "E431.bottom", {"start": v(42.74, 152.94) * mm, "end": v(41.78, 152.94) * mm});
            skLineSegment(sketch, "E431.top", {"start": v(42.74, 0) * mm, "end": v(41.78, 0) * mm});
            skLineSegment(sketch, "E431.left", {"start": v(42.74, 152.94) * mm, "end": v(42.74, 0) * mm});
            skLineSegment(sketch, "E431.right", {"start": v(41.78, 152.94) * mm, "end": v(41.78, 0) * mm});
            skSolve(sketch);
        }
        {
            var Q0;
            Q0 = qSketchRegion(id + "F43", true);
            extrude(context, id + "F44", {"entities" : qUnion([Q0]), "operationType" : NewBodyOperationType.ADD, "depth" : 2 * mm});
        }
        {
            var Q0;
            Q0=makeQuery(id+"F44.boolean.opBoolean","MERGE",FACE,{"derivedFrom":[makeQuery(id+"F40.opExtrude","SWEPT_FACE",FACE,{"disambiguationData":[OSD([sQuery(id+"F39.wireOp",EDGE,"E413.right")])]}),makeQuery(id+"F44.opExtrude","SWEPT_FACE",FACE,{"disambiguationData":[OSD([sQuery(id+"F43.wireOp",EDGE,"E429.right")])]})]});
            var sketch = newSketch(context, id + "F45", { "sketchPlane" : qUnion([Q0])});
            skLineSegment(sketch, "E432", {"start": v(5.71, -0.82) * mm, "end": v(6.7, -0.96) * mm});
            skLineSegment(sketch, "E433", {"start": v(6.7, -0.96) * mm, "end": v(28.4, 150.43) * mm});
            skLineSegment(sketch, "E434", {"start": v(6.7, -0.96) * mm, "end": v(7.56, 4.98) * mm});
            skLineSegment(sketch, "E435", {"start": v(7.56, 4.98) * mm, "end": v(8.4, 10.92) * mm});
            skLineSegment(sketch, "E436", {"start": v(8.4, 10.92) * mm, "end": v(9.26, 16.86) * mm});
            skLineSegment(sketch, "E437", {"start": v(9.26, 16.86) * mm, "end": v(10.1, 22.8) * mm});
            skLineSegment(sketch, "E438", {"start": v(10.1, 22.8) * mm, "end": v(10.96, 28.74) * mm});
            skLineSegment(sketch, "E439", {"start": v(10.96, 28.74) * mm, "end": v(11.81, 34.67) * mm});
            skLineSegment(sketch, "E440", {"start": v(11.81, 34.67) * mm, "end": v(12.66, 40.61) * mm});
            skLineSegment(sketch, "E441", {"start": v(12.66, 40.61) * mm, "end": v(13.51, 46.55) * mm});
            skLineSegment(sketch, "E442", {"start": v(13.51, 46.55) * mm, "end": v(14.37, 52.5) * mm});
            skLineSegment(sketch, "E443", {"start": v(14.37, 52.5) * mm, "end": v(15.22, 58.43) * mm});
            skLineSegment(sketch, "E444", {"start": v(15.22, 58.43) * mm, "end": v(16.07, 64.37) * mm});
            skLineSegment(sketch, "E445", {"start": v(16.07, 64.37) * mm, "end": v(16.92, 70.31) * mm});
            skLineSegment(sketch, "E446", {"start": v(16.92, 70.31) * mm, "end": v(17.77, 76.25) * mm});
            skLineSegment(sketch, "E447", {"start": v(17.77, 76.25) * mm, "end": v(18.62, 82.19) * mm});
            skLineSegment(sketch, "E448", {"start": v(18.62, 82.19) * mm, "end": v(19.47, 88.13) * mm});
            skLineSegment(sketch, "E449", {"start": v(19.47, 88.13) * mm, "end": v(20.33, 94.07) * mm});
            skLineSegment(sketch, "E450", {"start": v(20.33, 94.07) * mm, "end": v(21.18, 100) * mm});
            skLineSegment(sketch, "E451", {"start": v(21.18, 100) * mm, "end": v(22.03, 105.95) * mm});
            skLineSegment(sketch, "E452", {"start": v(22.03, 105.95) * mm, "end": v(22.88, 111.89) * mm});
            skLineSegment(sketch, "E453", {"start": v(22.88, 111.89) * mm, "end": v(23.73, 117.83) * mm});
            skLineSegment(sketch, "E454", {"start": v(23.73, 117.83) * mm, "end": v(24.58, 123.76) * mm});
            skLineSegment(sketch, "E455", {"start": v(24.58, 123.76) * mm, "end": v(25.43, 129.7) * mm});
            skLineSegment(sketch, "E456", {"start": v(25.43, 129.7) * mm, "end": v(26.28, 135.64) * mm});
            skLineSegment(sketch, "E457", {"start": v(26.28, 135.64) * mm, "end": v(27.14, 141.58) * mm});
            skLineSegment(sketch, "E458", {"start": v(27.14, 141.58) * mm, "end": v(27.99, 147.52) * mm});
            skPoint(sketch, "E459.middle", {"position": v(27.99, 147.52) * mm});
            skLineSegment(sketch, "E460", {"start": v(27.99, 147.52) * mm, "end": v(28.13, 148.51) * mm});
            skLineSegment(sketch, "E461", {"start": v(27.63, 148.58) * mm, "end": v(27.35, 146.6) * mm});
            skLineSegment(sketch, "E462", {"start": v(27.35, 146.6) * mm, "end": v(28.34, 146.46) * mm});
            skLineSegment(sketch, "E463", {"start": v(28.62, 148.44) * mm, "end": v(28.34, 146.46) * mm});
            skLineSegment(sketch, "E464", {"start": v(27.14, 141.58) * mm, "end": v(27.28, 142.57) * mm});
            skLineSegment(sketch, "E465", {"start": v(26.78, 142.64) * mm, "end": v(26.5, 140.66) * mm});
            skLineSegment(sketch, "E466", {"start": v(26.5, 140.66) * mm, "end": v(27.49, 140.52) * mm});
            skLineSegment(sketch, "E467", {"start": v(27.77, 142.5) * mm, "end": v(27.49, 140.52) * mm});
            skLineSegment(sketch, "E468", {"start": v(26.78, 142.64) * mm, "end": v(27.77, 142.5) * mm});
            skLineSegment(sketch, "E469", {"start": v(27.63, 148.58) * mm, "end": v(28.62, 148.44) * mm});
            skLineSegment(sketch, "E470", {"start": v(26.28, 135.64) * mm, "end": v(26.43, 136.63) * mm});
            skLineSegment(sketch, "E471", {"start": v(25.93, 136.7) * mm, "end": v(25.65, 134.72) * mm});
            skLineSegment(sketch, "E472", {"start": v(25.65, 134.72) * mm, "end": v(26.64, 134.58) * mm});
            skLineSegment(sketch, "E473", {"start": v(26.64, 134.58) * mm, "end": v(26.92, 136.56) * mm});
            skLineSegment(sketch, "E474", {"start": v(25.93, 136.7) * mm, "end": v(26.92, 136.56) * mm});
            skLineSegment(sketch, "E475", {"start": v(25.43, 129.7) * mm, "end": v(25.57, 130.7) * mm});
            skLineSegment(sketch, "E476", {"start": v(25.08, 130.76) * mm, "end": v(24.8, 128.78) * mm});
            skLineSegment(sketch, "E477", {"start": v(24.8, 128.78) * mm, "end": v(25.79, 128.64) * mm});
            skLineSegment(sketch, "E478", {"start": v(26.07, 130.62) * mm, "end": v(25.79, 128.64) * mm});
            skLineSegment(sketch, "E479", {"start": v(25.08, 130.76) * mm, "end": v(26.07, 130.62) * mm});
            skLineSegment(sketch, "E480", {"start": v(24.58, 123.76) * mm, "end": v(24.72, 124.75) * mm});
            skLineSegment(sketch, "E481", {"start": v(24.23, 124.83) * mm, "end": v(23.94, 122.85) * mm});
            skLineSegment(sketch, "E482", {"start": v(23.94, 122.85) * mm, "end": v(24.93, 122.7) * mm});
            skLineSegment(sketch, "E483", {"start": v(24.93, 122.7) * mm, "end": v(25.22, 124.68) * mm});
            skLineSegment(sketch, "E484", {"start": v(24.23, 124.83) * mm, "end": v(25.22, 124.68) * mm});
            skLineSegment(sketch, "E485", {"start": v(23.73, 117.83) * mm, "end": v(23.87, 118.81) * mm});
            skLineSegment(sketch, "E486", {"start": v(23.38, 118.89) * mm, "end": v(23.1, 116.9) * mm});
            skLineSegment(sketch, "E487", {"start": v(23.1, 116.9) * mm, "end": v(24.08, 116.76) * mm});
            skLineSegment(sketch, "E488", {"start": v(24.08, 116.76) * mm, "end": v(24.37, 118.74) * mm});
            skLineSegment(sketch, "E489", {"start": v(23.38, 118.89) * mm, "end": v(24.37, 118.74) * mm});
            skLineSegment(sketch, "E490", {"start": v(22.88, 111.89) * mm, "end": v(23.02, 112.88) * mm});
            skLineSegment(sketch, "E491", {"start": v(22.53, 112.95) * mm, "end": v(22.24, 110.97) * mm});
            skLineSegment(sketch, "E492", {"start": v(22.24, 110.97) * mm, "end": v(23.23, 110.82) * mm});
            skLineSegment(sketch, "E493", {"start": v(23.23, 110.82) * mm, "end": v(23.52, 112.8) * mm});
            skLineSegment(sketch, "E494", {"start": v(22.53, 112.95) * mm, "end": v(23.52, 112.8) * mm});
            skLineSegment(sketch, "E495", {"start": v(22.03, 105.95) * mm, "end": v(22.17, 106.94) * mm});
            skLineSegment(sketch, "E496", {"start": v(21.67, 107) * mm, "end": v(21.4, 105.03) * mm});
            skLineSegment(sketch, "E497", {"start": v(21.4, 105.03) * mm, "end": v(22.38, 104.89) * mm});
            skLineSegment(sketch, "E498", {"start": v(22.38, 104.89) * mm, "end": v(22.66, 106.87) * mm});
            skLineSegment(sketch, "E499", {"start": v(21.67, 107) * mm, "end": v(22.66, 106.87) * mm});
            skLineSegment(sketch, "E500", {"start": v(21.18, 100) * mm, "end": v(21.32, 101) * mm});
            skLineSegment(sketch, "E501", {"start": v(20.82, 101.07) * mm, "end": v(20.54, 99.09) * mm});
            skLineSegment(sketch, "E502", {"start": v(20.54, 99.09) * mm, "end": v(21.53, 98.95) * mm});
            skLineSegment(sketch, "E503", {"start": v(21.53, 98.95) * mm, "end": v(21.81, 100.93) * mm});
            skLineSegment(sketch, "E504", {"start": v(20.82, 101.07) * mm, "end": v(21.81, 100.93) * mm});
            skLineSegment(sketch, "E505", {"start": v(20.33, 94.07) * mm, "end": v(20.47, 95.06) * mm});
            skLineSegment(sketch, "E506", {"start": v(19.97, 95.13) * mm, "end": v(19.69, 93.15) * mm});
            skLineSegment(sketch, "E507", {"start": v(19.69, 93.15) * mm, "end": v(20.68, 93) * mm});
            skLineSegment(sketch, "E508", {"start": v(20.68, 93) * mm, "end": v(20.96, 94.99) * mm});
            skLineSegment(sketch, "E509", {"start": v(19.97, 95.13) * mm, "end": v(20.96, 94.99) * mm});
            skLineSegment(sketch, "E510", {"start": v(19.47, 88.13) * mm, "end": v(19.62, 89.12) * mm});
            skLineSegment(sketch, "E511", {"start": v(19.12, 89.19) * mm, "end": v(18.84, 87.2) * mm});
            skLineSegment(sketch, "E512", {"start": v(18.84, 87.2) * mm, "end": v(19.83, 87.07) * mm});
            skLineSegment(sketch, "E513", {"start": v(19.83, 87.07) * mm, "end": v(20.11, 89.05) * mm});
            skLineSegment(sketch, "E514", {"start": v(19.12, 89.19) * mm, "end": v(20.11, 89.05) * mm});
            skLineSegment(sketch, "E515", {"start": v(18.62, 82.19) * mm, "end": v(18.76, 83.18) * mm});
            skLineSegment(sketch, "E516", {"start": v(18.27, 83.25) * mm, "end": v(17.99, 81.27) * mm});
            skLineSegment(sketch, "E517", {"start": v(17.99, 81.27) * mm, "end": v(18.98, 81.13) * mm});
            skLineSegment(sketch, "E518", {"start": v(18.98, 81.13) * mm, "end": v(19.26, 83.1) * mm});
            skLineSegment(sketch, "E519", {"start": v(18.27, 83.25) * mm, "end": v(19.26, 83.1) * mm});
            skLineSegment(sketch, "E520", {"start": v(17.77, 76.25) * mm, "end": v(17.91, 77.24) * mm});
            skLineSegment(sketch, "E521", {"start": v(17.42, 77.31) * mm, "end": v(17.13, 75.33) * mm});
            skLineSegment(sketch, "E522", {"start": v(17.13, 75.33) * mm, "end": v(18.12, 75.19) * mm});
            skLineSegment(sketch, "E523", {"start": v(18.12, 75.19) * mm, "end": v(18.4, 77.17) * mm});
            skLineSegment(sketch, "E524", {"start": v(17.42, 77.31) * mm, "end": v(18.4, 77.17) * mm});
            skLineSegment(sketch, "E525", {"start": v(16.92, 70.31) * mm, "end": v(17.06, 71.3) * mm});
            skLineSegment(sketch, "E526", {"start": v(16.57, 71.37) * mm, "end": v(16.28, 69.4) * mm});
            skLineSegment(sketch, "E527", {"start": v(16.28, 69.4) * mm, "end": v(17.27, 69.25) * mm});
            skLineSegment(sketch, "E528", {"start": v(17.27, 69.25) * mm, "end": v(17.56, 71.23) * mm});
            skLineSegment(sketch, "E529", {"start": v(16.57, 71.37) * mm, "end": v(17.56, 71.23) * mm});
            skLineSegment(sketch, "E530", {"start": v(16.07, 64.37) * mm, "end": v(16.21, 65.36) * mm});
            skLineSegment(sketch, "E531", {"start": v(15.72, 65.43) * mm, "end": v(15.43, 63.45) * mm});
            skLineSegment(sketch, "E532", {"start": v(15.43, 63.45) * mm, "end": v(16.42, 63.31) * mm});
            skLineSegment(sketch, "E533", {"start": v(16.42, 63.31) * mm, "end": v(16.7, 65.3) * mm});
            skLineSegment(sketch, "E534", {"start": v(15.72, 65.43) * mm, "end": v(16.7, 65.3) * mm});
            skLineSegment(sketch, "E535", {"start": v(15.22, 58.43) * mm, "end": v(15.36, 59.42) * mm});
            skLineSegment(sketch, "E536", {"start": v(14.86, 59.5) * mm, "end": v(14.58, 57.51) * mm});
            skLineSegment(sketch, "E537", {"start": v(14.58, 57.51) * mm, "end": v(15.57, 57.37) * mm});
            skLineSegment(sketch, "E538", {"start": v(15.57, 57.37) * mm, "end": v(15.85, 59.35) * mm});
            skLineSegment(sketch, "E539", {"start": v(14.86, 59.5) * mm, "end": v(15.85, 59.35) * mm});
            skLineSegment(sketch, "E540", {"start": v(14.37, 52.5) * mm, "end": v(14.5, 53.48) * mm});
            skLineSegment(sketch, "E541", {"start": v(14.01, 53.55) * mm, "end": v(13.73, 51.57) * mm});
            skLineSegment(sketch, "E542", {"start": v(13.73, 51.57) * mm, "end": v(14.72, 51.43) * mm});
            skLineSegment(sketch, "E543", {"start": v(15, 53.41) * mm, "end": v(14.72, 51.43) * mm});
            skLineSegment(sketch, "E544", {"start": v(14.01, 53.55) * mm, "end": v(15, 53.41) * mm});
            skLineSegment(sketch, "E545", {"start": v(13.51, 46.55) * mm, "end": v(13.66, 47.54) * mm});
            skLineSegment(sketch, "E546", {"start": v(13.16, 47.61) * mm, "end": v(12.88, 45.63) * mm});
            skLineSegment(sketch, "E547", {"start": v(12.88, 45.63) * mm, "end": v(13.87, 45.5) * mm});
            skLineSegment(sketch, "E548", {"start": v(13.87, 45.5) * mm, "end": v(14.15, 47.47) * mm});
            skLineSegment(sketch, "E549", {"start": v(13.16, 47.61) * mm, "end": v(14.15, 47.47) * mm});
            skLineSegment(sketch, "E550", {"start": v(12.66, 40.61) * mm, "end": v(12.8, 41.6) * mm});
            skLineSegment(sketch, "E551", {"start": v(12.31, 41.67) * mm, "end": v(12.03, 39.7) * mm});
            skLineSegment(sketch, "E552", {"start": v(12.03, 39.7) * mm, "end": v(13.02, 39.55) * mm});
            skLineSegment(sketch, "E553", {"start": v(13.02, 39.55) * mm, "end": v(13.3, 41.53) * mm});
            skLineSegment(sketch, "E554", {"start": v(12.31, 41.67) * mm, "end": v(13.3, 41.53) * mm});
            skLineSegment(sketch, "E555", {"start": v(11.81, 34.67) * mm, "end": v(11.95, 35.66) * mm});
            skLineSegment(sketch, "E556", {"start": v(11.46, 35.74) * mm, "end": v(11.18, 33.76) * mm});
            skLineSegment(sketch, "E557", {"start": v(11.18, 33.76) * mm, "end": v(12.17, 33.61) * mm});
            skLineSegment(sketch, "E558", {"start": v(12.17, 33.61) * mm, "end": v(12.45, 35.6) * mm});
            skLineSegment(sketch, "E559", {"start": v(11.46, 35.74) * mm, "end": v(12.45, 35.6) * mm});
            skLineSegment(sketch, "E560", {"start": v(10.96, 28.74) * mm, "end": v(11.1, 29.73) * mm});
            skLineSegment(sketch, "E561", {"start": v(10.6, 29.8) * mm, "end": v(10.32, 27.82) * mm});
            skLineSegment(sketch, "E562", {"start": v(10.32, 27.82) * mm, "end": v(11.31, 27.67) * mm});
            skLineSegment(sketch, "E563", {"start": v(11.31, 27.67) * mm, "end": v(11.6, 29.65) * mm});
            skLineSegment(sketch, "E564", {"start": v(10.6, 29.8) * mm, "end": v(11.6, 29.65) * mm});
            skLineSegment(sketch, "E565", {"start": v(10.1, 22.8) * mm, "end": v(10.25, 23.79) * mm});
            skLineSegment(sketch, "E566", {"start": v(9.76, 23.86) * mm, "end": v(9.47, 21.88) * mm});
            skLineSegment(sketch, "E567", {"start": v(9.47, 21.88) * mm, "end": v(10.46, 21.74) * mm});
            skLineSegment(sketch, "E568", {"start": v(10.46, 21.74) * mm, "end": v(10.75, 23.72) * mm});
            skLineSegment(sketch, "E569", {"start": v(9.76, 23.86) * mm, "end": v(10.75, 23.72) * mm});
            skLineSegment(sketch, "E570", {"start": v(9.26, 16.86) * mm, "end": v(9.4, 17.85) * mm});
            skLineSegment(sketch, "E571", {"start": v(8.9, 17.92) * mm, "end": v(8.62, 15.94) * mm});
            skLineSegment(sketch, "E572", {"start": v(8.62, 15.94) * mm, "end": v(9.61, 15.8) * mm});
            skLineSegment(sketch, "E573", {"start": v(9.61, 15.8) * mm, "end": v(9.9, 17.78) * mm});
            skLineSegment(sketch, "E574", {"start": v(8.9, 17.92) * mm, "end": v(9.9, 17.78) * mm});
            skLineSegment(sketch, "E575", {"start": v(8.4, 10.92) * mm, "end": v(8.55, 11.9) * mm});
            skLineSegment(sketch, "E576", {"start": v(8.05, 11.98) * mm, "end": v(7.77, 10) * mm});
            skLineSegment(sketch, "E577", {"start": v(7.77, 10) * mm, "end": v(8.76, 9.86) * mm});
            skLineSegment(sketch, "E578", {"start": v(8.76, 9.86) * mm, "end": v(9.04, 11.84) * mm});
            skLineSegment(sketch, "E579", {"start": v(8.05, 11.98) * mm, "end": v(9.04, 11.84) * mm});
            skLineSegment(sketch, "E580", {"start": v(7.56, 4.98) * mm, "end": v(7.7, 5.97) * mm});
            skLineSegment(sketch, "E581", {"start": v(7.2, 6.04) * mm, "end": v(6.92, 4.06) * mm});
            skLineSegment(sketch, "E582", {"start": v(6.92, 4.06) * mm, "end": v(7.9, 3.92) * mm});
            skLineSegment(sketch, "E583", {"start": v(7.9, 3.92) * mm, "end": v(8.2, 5.9) * mm});
            skLineSegment(sketch, "E584", {"start": v(7.2, 6.04) * mm, "end": v(8.2, 5.9) * mm});
            skSolve(sketch);
        }
        {
            var Q0;
            Q0 = qSketchRegion(id + "F45", true);
            var Q1;
            Q1=makeQuery(id+"F44.opExtrude","SWEPT_FACE",FACE,{"disambiguationData":[OSD([sQuery(id+"F43.wireOp",EDGE,"E431.right")])]});
            extrude(context, id + "F46", {"entities" : qUnion([Q0]), "operationType" : NewBodyOperationType.ADD, "endBound" : BoundingType.UP_TO_SURFACE, "endBoundEntityFace" : qUnion([Q1]), "depth" : 25 * mm});
        }
    });
